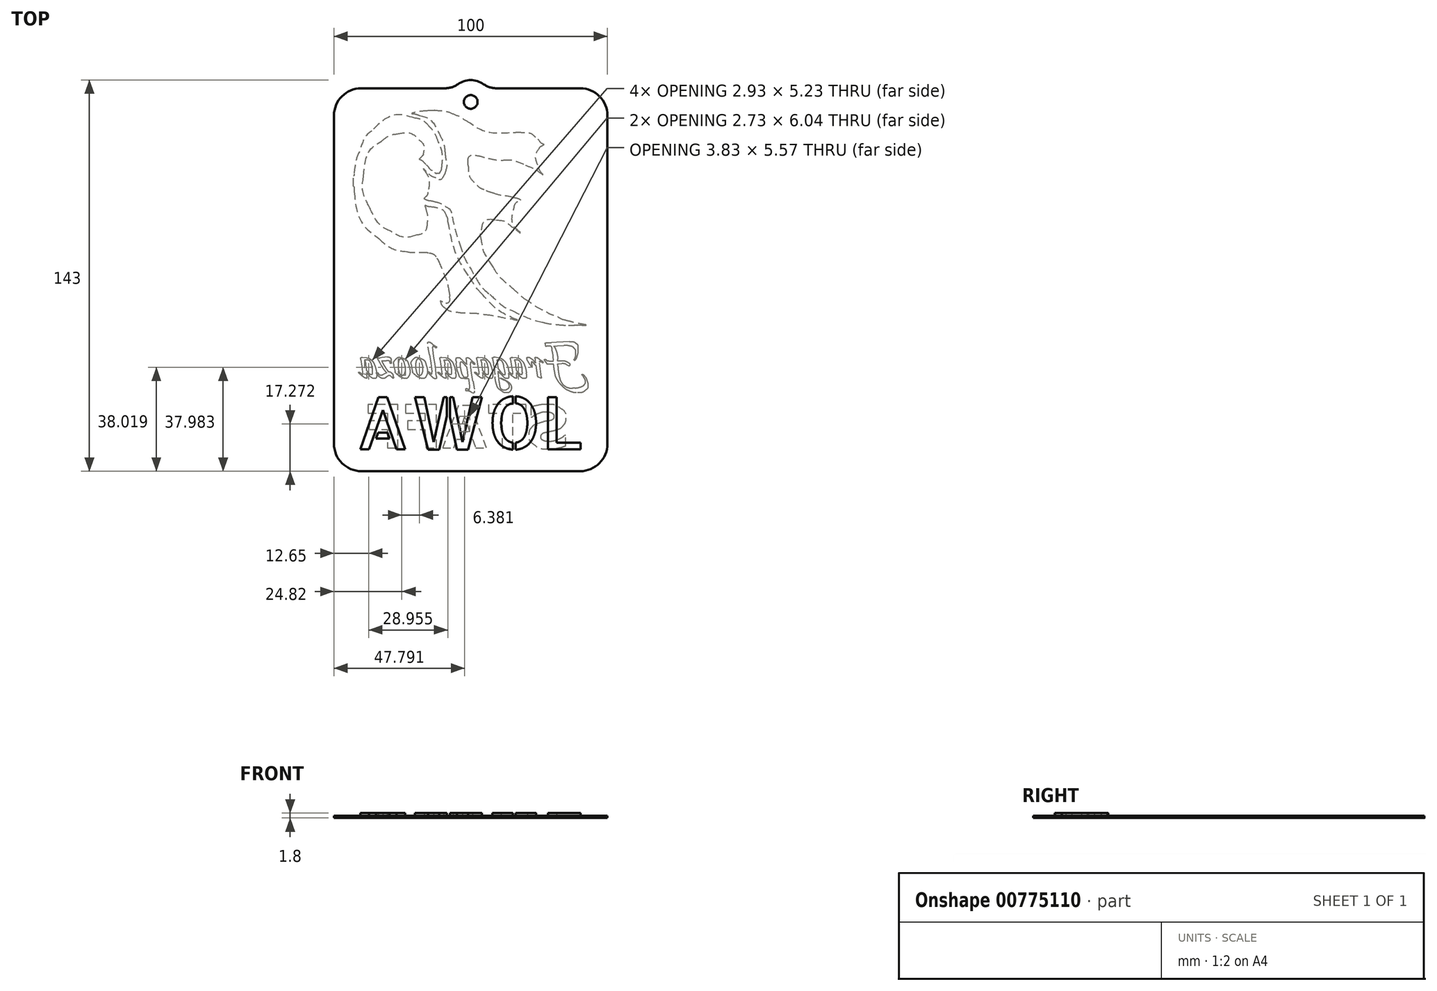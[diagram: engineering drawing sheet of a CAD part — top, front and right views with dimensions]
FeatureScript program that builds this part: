
annotation { "Feature Type Name" : "Feature", "Feature Type Description" : "" }
export const myFeature = defineFeature(function(context is Context, id is Id, definition is map)
    precondition{}
    {
        {
            var Q0;
            Q0=qCreatedBy(makeId("Top.planeOp"),FACE);
            var sketch = newSketch(context, id + "F0", { "sketchPlane" : qUnion([Q0])});
            skLineSegment(sketch, "E0.bottom", {"start": v(-40, 70) * mm, "end": v(-9.33, 70) * mm});
            skLineSegment(sketch, "E0.top", {"start": v(-40, -70) * mm, "end": v(40, -70) * mm});
            skLineSegment(sketch, "E0.left", {"start": v(-50, 60) * mm, "end": v(-50, -60) * mm});
            skLineSegment(sketch, "E0.right", {"start": v(50, 60) * mm, "end": v(50, -60) * mm});
            skPoint(sketch, "E0.middle", {"position": v(0, 0) * mm});
            skCircle(sketch, "E1", {"center": v(0, 65) * mm, "radius": 2.5 * mm});
            skPoint(sketch, "E2.visualSharp", {"position": v(-50, 70) * mm});
            skArc(sketch, "E2.filletArc", {"start": v(-40, 70) * mm, "mid": v(-47.07, 67.07) * mm, "end": v(-50, 60) * mm});
            skPoint(sketch, "E3.visualSharp", {"position": v(50, 70) * mm});
            skArc(sketch, "E3.filletArc", {"start": v(50, 60) * mm, "mid": v(47.07, 67.07) * mm, "end": v(40, 70) * mm});
            skPoint(sketch, "E4.visualSharp", {"position": v(50, -70) * mm});
            skArc(sketch, "E4.filletArc", {"start": v(40, -70) * mm, "mid": v(47.07, -67.07) * mm, "end": v(50, -60) * mm});
            skPoint(sketch, "E5.visualSharp", {"position": v(-50, -70) * mm});
            skArc(sketch, "E5.filletArc", {"start": v(-50, -60) * mm, "mid": v(-47.07, -67.07) * mm, "end": v(-40, -70) * mm});
            skArc(sketch, "E6", {"start": v(-4.66, 71.5) * mm, "mid": v(0, 73) * mm, "end": v(4.66, 71.5) * mm});
            skArc(sketch, "E7.filletArc", {"start": v(-9.33, 70) * mm, "mid": v(-6.88, 70.38) * mm, "end": v(-4.66, 71.5) * mm});
            skLineSegment(sketch, "E8", {"start": v(40, 70) * mm, "end": v(9.33, 70) * mm});
            skArc(sketch, "E9.filletArc", {"start": v(4.66, 71.5) * mm, "mid": v(6.88, 70.38) * mm, "end": v(9.33, 70) * mm});
            skSolve(sketch);
        }
        {
            var Q0;
            Q0=qCreatedBy(makeId("Top.planeOp"),FACE);
            var sketch = newSketch(context, id + "F1", { "sketchPlane" : qUnion([Q0])});
            skLineSegment(sketch, "E10", {"start": v(38.17, -16.7) * mm, "end": v(38.78, -16.7) * mm});
            skLineSegment(sketch, "E11", {"start": v(-13.07, 61.96) * mm, "end": v(-13.17, 61.96) * mm});
            skLineSegment(sketch, "E12", {"start": v(-14.17, 61.96) * mm, "end": v(-14.37, 61.96) * mm});
            skLineSegment(sketch, "E13", {"start": v(-42.85, 37.93) * mm, "end": v(-42.85, 36.81) * mm});
            skLineSegment(sketch, "E14", {"start": v(-42.85, 35.49) * mm, "end": v(-42.85, 34.98) * mm});
            skLineSegment(sketch, "E15", {"start": v(-42.85, 34.78) * mm, "end": v(-42.85, 34.16) * mm});
            skLineSegment(sketch, "E16", {"start": v(40.64, -16.7) * mm, "end": v(40.63, -16.62) * mm});
            skLineSegment(sketch, "E17", {"start": v(38.83, -16.7) * mm, "end": v(40.64, -16.7) * mm});
            skLineSegment(sketch, "E18", {"start": v(-42.85, 36.81) * mm, "end": v(-42.85, 35.49) * mm});
            skLineSegment(sketch, "E19", {"start": v(-13.21, 61.96) * mm, "end": v(-14.22, 61.96) * mm});
            skLineSegment(sketch, "E20", {"start": v(-42.85, 34.98) * mm, "end": v(-42.85, 34.77) * mm});
            skLineSegment(sketch, "E21", {"start": v(36.03, -31.52) * mm, "end": v(35.01, -30.98) * mm});
            skLineSegment(sketch, "E22", {"start": v(33.37, -30.7) * mm, "end": v(32.17, -30.75) * mm});
            skLineSegment(sketch, "E23", {"start": v(32.17, -30.75) * mm, "end": v(30.92, -30.82) * mm});
            skLineSegment(sketch, "E24", {"start": v(30.92, -30.82) * mm, "end": v(27.9, -30.82) * mm});
            skLineSegment(sketch, "E25", {"start": v(27.9, -30.82) * mm, "end": v(27.52, -30.26) * mm});
            skLineSegment(sketch, "E26", {"start": v(26.88, -29.35) * mm, "end": v(26.9, -29.28) * mm});
            skLineSegment(sketch, "E27", {"start": v(30.32, -29.76) * mm, "end": v(31.57, -29.76) * mm});
            skLineSegment(sketch, "E28", {"start": v(31.57, -29.76) * mm, "end": v(33.15, -29.76) * mm});
            skLineSegment(sketch, "E29", {"start": v(33.15, -29.76) * mm, "end": v(34.41, -29.76) * mm});
            skLineSegment(sketch, "E30", {"start": v(34.05, -24.06) * mm, "end": v(31.6, -24.16) * mm});
            skLineSegment(sketch, "E31", {"start": v(31.6, -24.16) * mm, "end": v(29.36, -24.3) * mm});
            skLineSegment(sketch, "E32", {"start": v(27.3, -24.39) * mm, "end": v(27.09, -23.13) * mm});
            skLineSegment(sketch, "E33", {"start": v(29.45, -22.97) * mm, "end": v(31.35, -22.93) * mm});
            skLineSegment(sketch, "E34", {"start": v(31.35, -22.93) * mm, "end": v(33.78, -22.78) * mm});
            skLineSegment(sketch, "E35", {"start": v(33.78, -22.78) * mm, "end": v(36.14, -22.66) * mm});
            skLineSegment(sketch, "E36", {"start": v(38.04, -29.5) * mm, "end": v(37.7, -29.32) * mm});
            skLineSegment(sketch, "E37", {"start": v(30.25, -30.2) * mm, "end": v(29.88, -26.54) * mm});
            skLineSegment(sketch, "E38", {"start": v(29.55, -24.56) * mm, "end": v(29.3, -24.3) * mm});
            skLineSegment(sketch, "E39", {"start": v(29.18, -23.96) * mm, "end": v(29.55, -24.04) * mm});
            skLineSegment(sketch, "E40", {"start": v(31.76, -29.06) * mm, "end": v(31.88, -31.82) * mm});
            skLineSegment(sketch, "E41", {"start": v(37.27, -39.71) * mm, "end": v(38.3, -39.63) * mm});
            skLineSegment(sketch, "E42", {"start": v(41.15, -35.4) * mm, "end": v(40.78, -34.92) * mm});
            skLineSegment(sketch, "E43", {"start": v(40.78, -34.92) * mm, "end": v(40.72, -34.76) * mm});
            skLineSegment(sketch, "E44", {"start": v(23.56, -29.53) * mm, "end": v(23.5, -28.89) * mm});
            skLineSegment(sketch, "E45", {"start": v(24.23, -28.54) * mm, "end": v(25.22, -29.23) * mm});
            skLineSegment(sketch, "E46", {"start": v(25.22, -29.23) * mm, "end": v(26.33, -30.01) * mm});
            skLineSegment(sketch, "E47", {"start": v(26.48, -30.3) * mm, "end": v(26.4, -30.34) * mm});
            skLineSegment(sketch, "E48", {"start": v(26.4, -30.34) * mm, "end": v(26.3, -30.32) * mm});
            skLineSegment(sketch, "E49", {"start": v(26.3, -30.32) * mm, "end": v(26.17, -30.3) * mm});
            skLineSegment(sketch, "E50", {"start": v(25.15, -30.3) * mm, "end": v(25.53, -33.54) * mm});
            skLineSegment(sketch, "E51", {"start": v(25.53, -33.54) * mm, "end": v(25.79, -35.64) * mm});
            skLineSegment(sketch, "E52", {"start": v(25.88, -36) * mm, "end": v(24.4, -35.44) * mm});
            skLineSegment(sketch, "E53", {"start": v(23.19, -29.85) * mm, "end": v(23.89, -30.75) * mm});
            skLineSegment(sketch, "E54", {"start": v(23.65, -31.18) * mm, "end": v(23.19, -30.77) * mm});
            skLineSegment(sketch, "E55", {"start": v(15.9, -29.4) * mm, "end": v(15.4, -29.4) * mm});
            skLineSegment(sketch, "E56", {"start": v(15.4, -29.4) * mm, "end": v(15.02, -29.33) * mm});
            skLineSegment(sketch, "E57", {"start": v(15.24, -28.42) * mm, "end": v(16.71, -28.55) * mm});
            skLineSegment(sketch, "E58", {"start": v(17.3, -34.56) * mm, "end": v(16.63, -33.84) * mm});
            skLineSegment(sketch, "E59", {"start": v(16.01, -32.3) * mm, "end": v(16.46, -32.84) * mm});
            skLineSegment(sketch, "E60", {"start": v(16.96, -29.4) * mm, "end": v(16.5, -29.4) * mm});
            skLineSegment(sketch, "E61", {"start": v(16.5, -29.4) * mm, "end": v(15.9, -29.4) * mm});
            skLineSegment(sketch, "E62", {"start": v(16.38, -31.1) * mm, "end": v(16.6, -32.79) * mm});
            skLineSegment(sketch, "E63", {"start": v(16.6, -32.79) * mm, "end": v(16.8, -34.4) * mm});
            skLineSegment(sketch, "E64", {"start": v(16.8, -34.4) * mm, "end": v(16.85, -35.3) * mm});
            skLineSegment(sketch, "E65", {"start": v(14.85, -34.45) * mm, "end": v(15.26, -34.75) * mm});
            skLineSegment(sketch, "E66", {"start": v(15.33, -34.51) * mm, "end": v(15.26, -33.72) * mm});
            skLineSegment(sketch, "E67", {"start": v(15.26, -33.72) * mm, "end": v(14.93, -31.64) * mm});
            skLineSegment(sketch, "E68", {"start": v(14.93, -31.64) * mm, "end": v(14.54, -29.14) * mm});
            skLineSegment(sketch, "E69", {"start": v(9.13, -29.4) * mm, "end": v(8.63, -29.4) * mm});
            skLineSegment(sketch, "E70", {"start": v(8.63, -29.4) * mm, "end": v(8.27, -29.31) * mm});
            skLineSegment(sketch, "E71", {"start": v(8.04, -29.08) * mm, "end": v(7.89, -28.74) * mm});
            skLineSegment(sketch, "E72", {"start": v(8.47, -28.35) * mm, "end": v(8.95, -28.35) * mm});
            skLineSegment(sketch, "E73", {"start": v(8.95, -28.35) * mm, "end": v(9.46, -28.52) * mm});
            skLineSegment(sketch, "E74", {"start": v(9.46, -28.52) * mm, "end": v(10.14, -28.6) * mm});
            skLineSegment(sketch, "E75", {"start": v(11.28, -34.74) * mm, "end": v(10.47, -33.88) * mm});
            skLineSegment(sketch, "E76", {"start": v(9.69, -32.05) * mm, "end": v(10.37, -32.95) * mm});
            skLineSegment(sketch, "E77", {"start": v(10.37, -32.95) * mm, "end": v(11.14, -33.94) * mm});
            skLineSegment(sketch, "E78", {"start": v(12.6, -34.13) * mm, "end": v(12.52, -33.32) * mm});
            skLineSegment(sketch, "E79", {"start": v(12.52, -33.32) * mm, "end": v(12.29, -32.26) * mm});
            skLineSegment(sketch, "E80", {"start": v(12.29, -32.26) * mm, "end": v(12.13, -31.6) * mm});
            skLineSegment(sketch, "E81", {"start": v(10.33, -29.4) * mm, "end": v(9.77, -29.4) * mm});
            skLineSegment(sketch, "E82", {"start": v(9.77, -29.4) * mm, "end": v(9.13, -29.4) * mm});
            skLineSegment(sketch, "E83", {"start": v(9.46, -28.84) * mm, "end": v(9.77, -30.97) * mm});
            skLineSegment(sketch, "E84", {"start": v(9.77, -30.97) * mm, "end": v(10.1, -34.04) * mm});
            skLineSegment(sketch, "E85", {"start": v(10.1, -34.04) * mm, "end": v(10.34, -36.29) * mm});
            skLineSegment(sketch, "E86", {"start": v(10.34, -36.29) * mm, "end": v(10.47, -37.68) * mm});
            skLineSegment(sketch, "E87", {"start": v(12.25, -36.7) * mm, "end": v(11.22, -36.28) * mm});
            skLineSegment(sketch, "E88", {"start": v(10.66, -36) * mm, "end": v(10.7, -35.94) * mm});
            skLineSegment(sketch, "E89", {"start": v(8.88, -35.3) * mm, "end": v(8.5, -31.75) * mm});
            skLineSegment(sketch, "E90", {"start": v(3.54, -29.4) * mm, "end": v(3.04, -29.4) * mm});
            skLineSegment(sketch, "E91", {"start": v(3.04, -29.4) * mm, "end": v(2.67, -29.33) * mm});
            skLineSegment(sketch, "E92", {"start": v(2.88, -28.42) * mm, "end": v(4.36, -28.55) * mm});
            skLineSegment(sketch, "E93", {"start": v(4.94, -34.56) * mm, "end": v(4.28, -33.84) * mm});
            skLineSegment(sketch, "E94", {"start": v(3.66, -32.3) * mm, "end": v(4.1, -32.84) * mm});
            skLineSegment(sketch, "E95", {"start": v(4.6, -29.4) * mm, "end": v(4.14, -29.4) * mm});
            skLineSegment(sketch, "E96", {"start": v(4.14, -29.4) * mm, "end": v(3.54, -29.4) * mm});
            skLineSegment(sketch, "E97", {"start": v(4.02, -31.1) * mm, "end": v(4.25, -32.79) * mm});
            skLineSegment(sketch, "E98", {"start": v(4.25, -32.79) * mm, "end": v(4.44, -34.4) * mm});
            skLineSegment(sketch, "E99", {"start": v(4.44, -34.4) * mm, "end": v(4.5, -35.3) * mm});
            skLineSegment(sketch, "E100", {"start": v(2.5, -34.45) * mm, "end": v(2.9, -34.75) * mm});
            skLineSegment(sketch, "E101", {"start": v(2.98, -34.51) * mm, "end": v(2.9, -33.72) * mm});
            skLineSegment(sketch, "E102", {"start": v(2.9, -33.72) * mm, "end": v(2.58, -31.64) * mm});
            skLineSegment(sketch, "E103", {"start": v(2.58, -31.64) * mm, "end": v(2.19, -29.14) * mm});
            skLineSegment(sketch, "E104", {"start": v(-0.07, -30.77) * mm, "end": v(0.03, -32.01) * mm});
            skLineSegment(sketch, "E105", {"start": v(0.03, -32.01) * mm, "end": v(0.35, -34.14) * mm});
            skLineSegment(sketch, "E106", {"start": v(0.35, -34.14) * mm, "end": v(0.85, -37.11) * mm});
            skLineSegment(sketch, "E107", {"start": v(0.96, -41.4) * mm, "end": v(0.32, -41.16) * mm});
            skLineSegment(sketch, "E108", {"start": v(-0.43, -39.67) * mm, "end": v(-0.47, -38.83) * mm});
            skLineSegment(sketch, "E109", {"start": v(-0.47, -38.83) * mm, "end": v(-0.77, -36.7) * mm});
            skLineSegment(sketch, "E110", {"start": v(-0.77, -36.7) * mm, "end": v(-1.14, -33.74) * mm});
            skLineSegment(sketch, "E111", {"start": v(-1.14, -33.74) * mm, "end": v(-1.34, -32.16) * mm});
            skLineSegment(sketch, "E112", {"start": v(-1.34, -32.16) * mm, "end": v(-1.56, -30.34) * mm});
            skLineSegment(sketch, "E113", {"start": v(-1.56, -30.34) * mm, "end": v(-1.62, -29.37) * mm});
            skLineSegment(sketch, "E114", {"start": v(-0.41, -35.45) * mm, "end": v(-0.36, -35.65) * mm});
            skLineSegment(sketch, "E115", {"start": v(-0.18, -36.1) * mm, "end": v(-0.24, -36.16) * mm});
            skLineSegment(sketch, "E116", {"start": v(-0.24, -36.16) * mm, "end": v(-0.31, -36.19) * mm});
            skLineSegment(sketch, "E117", {"start": v(-0.31, -36.19) * mm, "end": v(-0.7, -36.11) * mm});
            skLineSegment(sketch, "E118", {"start": v(-0.7, -36.11) * mm, "end": v(-1.4, -36.11) * mm});
            skLineSegment(sketch, "E119", {"start": v(-1.4, -36.11) * mm, "end": v(-2.27, -36.11) * mm});
            skLineSegment(sketch, "E120", {"start": v(-2.53, -30.03) * mm, "end": v(-1.85, -30.67) * mm});
            skLineSegment(sketch, "E121", {"start": v(-9.94, -29.4) * mm, "end": v(-10.44, -29.4) * mm});
            skLineSegment(sketch, "E122", {"start": v(-10.44, -29.4) * mm, "end": v(-10.8, -29.33) * mm});
            skLineSegment(sketch, "E123", {"start": v(-10.6, -28.42) * mm, "end": v(-9.12, -28.55) * mm});
            skLineSegment(sketch, "E124", {"start": v(-8.54, -34.56) * mm, "end": v(-9.2, -33.84) * mm});
            skLineSegment(sketch, "E125", {"start": v(-9.82, -32.3) * mm, "end": v(-9.37, -32.84) * mm});
            skLineSegment(sketch, "E126", {"start": v(-8.87, -29.4) * mm, "end": v(-9.34, -29.4) * mm});
            skLineSegment(sketch, "E127", {"start": v(-9.34, -29.4) * mm, "end": v(-9.94, -29.4) * mm});
            skLineSegment(sketch, "E128", {"start": v(-9.46, -31.1) * mm, "end": v(-9.23, -32.79) * mm});
            skLineSegment(sketch, "E129", {"start": v(-9.23, -32.79) * mm, "end": v(-9.04, -34.4) * mm});
            skLineSegment(sketch, "E130", {"start": v(-9.04, -34.4) * mm, "end": v(-8.99, -35.3) * mm});
            skLineSegment(sketch, "E131", {"start": v(-10.98, -34.45) * mm, "end": v(-10.58, -34.75) * mm});
            skLineSegment(sketch, "E132", {"start": v(-10.5, -34.51) * mm, "end": v(-10.58, -33.72) * mm});
            skLineSegment(sketch, "E133", {"start": v(-10.58, -33.72) * mm, "end": v(-10.9, -31.64) * mm});
            skLineSegment(sketch, "E134", {"start": v(-10.9, -31.64) * mm, "end": v(-11.29, -29.14) * mm});
            skLineSegment(sketch, "E135", {"start": v(-14.16, -33.74) * mm, "end": v(-14.26, -32.52) * mm});
            skLineSegment(sketch, "E136", {"start": v(-14.26, -32.52) * mm, "end": v(-14.56, -30.46) * mm});
            skLineSegment(sketch, "E137", {"start": v(-14.56, -30.46) * mm, "end": v(-15.08, -27.43) * mm});
            skLineSegment(sketch, "E138", {"start": v(-15, -22.92) * mm, "end": v(-14.03, -23.56) * mm});
            skLineSegment(sketch, "E139", {"start": v(-12.63, -24.87) * mm, "end": v(-12.86, -24.8) * mm});
            skLineSegment(sketch, "E140", {"start": v(-13.91, -24.76) * mm, "end": v(-13.85, -25.5) * mm});
            skLineSegment(sketch, "E141", {"start": v(-13.85, -25.5) * mm, "end": v(-13.65, -26.9) * mm});
            skLineSegment(sketch, "E142", {"start": v(-13.65, -26.9) * mm, "end": v(-13.36, -28.73) * mm});
            skLineSegment(sketch, "E143", {"start": v(-13.36, -28.73) * mm, "end": v(-13.08, -30.79) * mm});
            skLineSegment(sketch, "E144", {"start": v(-13.08, -30.79) * mm, "end": v(-12.8, -32.84) * mm});
            skLineSegment(sketch, "E145", {"start": v(-12.8, -32.84) * mm, "end": v(-12.61, -34.45) * mm});
            skLineSegment(sketch, "E146", {"start": v(-12.61, -34.45) * mm, "end": v(-12.55, -35.39) * mm});
            skLineSegment(sketch, "E147", {"start": v(-19.13, -35.54) * mm, "end": v(-20.12, -34.9) * mm});
            skLineSegment(sketch, "E148", {"start": v(-21.26, -33.55) * mm, "end": v(-21.5, -32.5) * mm});
            skLineSegment(sketch, "E149", {"start": v(-21.5, -32.5) * mm, "end": v(-21.73, -31.52) * mm});
            skLineSegment(sketch, "E150", {"start": v(-21.73, -31.52) * mm, "end": v(-21.79, -30.84) * mm});
            skLineSegment(sketch, "E151", {"start": v(-19.8, -28.37) * mm, "end": v(-19.36, -28.42) * mm});
            skLineSegment(sketch, "E152", {"start": v(-19.36, -28.42) * mm, "end": v(-18.37, -28.75) * mm});
            skLineSegment(sketch, "E153", {"start": v(-17.54, -31.66) * mm, "end": v(-18, -30.05) * mm});
            skLineSegment(sketch, "E154", {"start": v(-25.5, -35.54) * mm, "end": v(-26.5, -34.9) * mm});
            skLineSegment(sketch, "E155", {"start": v(-27.64, -33.55) * mm, "end": v(-27.88, -32.5) * mm});
            skLineSegment(sketch, "E156", {"start": v(-27.88, -32.5) * mm, "end": v(-28.1, -31.52) * mm});
            skLineSegment(sketch, "E157", {"start": v(-28.1, -31.52) * mm, "end": v(-28.17, -30.84) * mm});
            skLineSegment(sketch, "E158", {"start": v(-26.19, -28.37) * mm, "end": v(-25.74, -28.42) * mm});
            skLineSegment(sketch, "E159", {"start": v(-25.74, -28.42) * mm, "end": v(-24.75, -28.75) * mm});
            skLineSegment(sketch, "E160", {"start": v(-23.92, -31.66) * mm, "end": v(-24.38, -30.05) * mm});
            skLineSegment(sketch, "E161", {"start": v(-30.82, -29.63) * mm, "end": v(-31.6, -29.66) * mm});
            skLineSegment(sketch, "E162", {"start": v(-31.6, -29.66) * mm, "end": v(-32.28, -29.63) * mm});
            skLineSegment(sketch, "E163", {"start": v(-32.28, -29.63) * mm, "end": v(-32.6, -29.59) * mm});
            skLineSegment(sketch, "E164", {"start": v(-28.05, -35.7) * mm, "end": v(-28.34, -36) * mm});
            skLineSegment(sketch, "E165", {"start": v(-32.16, -32.19) * mm, "end": v(-32.67, -31.4) * mm});
            skLineSegment(sketch, "E166", {"start": v(-32.67, -31.4) * mm, "end": v(-33.23, -30.44) * mm});
            skLineSegment(sketch, "E167", {"start": v(-33.23, -30.44) * mm, "end": v(-33.8, -29.45) * mm});
            skLineSegment(sketch, "E168", {"start": v(-33.8, -29.45) * mm, "end": v(-34.28, -28.64) * mm});
            skLineSegment(sketch, "E169", {"start": v(-34.18, -28.33) * mm, "end": v(-34.02, -28.38) * mm});
            skLineSegment(sketch, "E170", {"start": v(-33.17, -28.56) * mm, "end": v(-32.43, -28.52) * mm});
            skLineSegment(sketch, "E171", {"start": v(-32.43, -28.52) * mm, "end": v(-31.52, -28.4) * mm});
            skLineSegment(sketch, "E172", {"start": v(-31.52, -28.4) * mm, "end": v(-30.4, -28.23) * mm});
            skLineSegment(sketch, "E173", {"start": v(-29.1, -29.33) * mm, "end": v(-29.02, -30) * mm});
            skLineSegment(sketch, "E174", {"start": v(-28.09, -35.68) * mm, "end": v(-28.22, -35.85) * mm});
            skLineSegment(sketch, "E175", {"start": v(-28.4, -35.95) * mm, "end": v(-29.27, -35.27) * mm});
            skLineSegment(sketch, "E176", {"start": v(-32.12, -34.67) * mm, "end": v(-31.13, -34.22) * mm});
            skLineSegment(sketch, "E177", {"start": v(-31.13, -34.22) * mm, "end": v(-30.22, -33.8) * mm});
            skLineSegment(sketch, "E178", {"start": v(-28.36, -35.08) * mm, "end": v(-28.32, -35.29) * mm});
            skLineSegment(sketch, "E179", {"start": v(-28.32, -35.29) * mm, "end": v(-28.26, -35.48) * mm});
            skLineSegment(sketch, "E180", {"start": v(-28.26, -35.48) * mm, "end": v(-28.09, -35.68) * mm});
            skLineSegment(sketch, "E181", {"start": v(-38.9, -29.4) * mm, "end": v(-39.4, -29.4) * mm});
            skLineSegment(sketch, "E182", {"start": v(-39.4, -29.4) * mm, "end": v(-39.76, -29.33) * mm});
            skLineSegment(sketch, "E183", {"start": v(-39.55, -28.42) * mm, "end": v(-38.08, -28.55) * mm});
            skLineSegment(sketch, "E184", {"start": v(-37.5, -34.56) * mm, "end": v(-38.15, -33.84) * mm});
            skLineSegment(sketch, "E185", {"start": v(-38.77, -32.3) * mm, "end": v(-38.33, -32.84) * mm});
            skLineSegment(sketch, "E186", {"start": v(-37.82, -29.4) * mm, "end": v(-38.3, -29.4) * mm});
            skLineSegment(sketch, "E187", {"start": v(-38.3, -29.4) * mm, "end": v(-38.9, -29.4) * mm});
            skLineSegment(sketch, "E188", {"start": v(-38.41, -31.1) * mm, "end": v(-38.19, -32.79) * mm});
            skLineSegment(sketch, "E189", {"start": v(-38.19, -32.79) * mm, "end": v(-38, -34.4) * mm});
            skLineSegment(sketch, "E190", {"start": v(-38, -34.4) * mm, "end": v(-37.94, -35.3) * mm});
            skLineSegment(sketch, "E191", {"start": v(-39.94, -34.45) * mm, "end": v(-39.53, -34.75) * mm});
            skLineSegment(sketch, "E192", {"start": v(-39.45, -34.51) * mm, "end": v(-39.53, -33.72) * mm});
            skLineSegment(sketch, "E193", {"start": v(-39.53, -33.72) * mm, "end": v(-39.86, -31.64) * mm});
            skLineSegment(sketch, "E194", {"start": v(-39.86, -31.64) * mm, "end": v(-40.24, -29.14) * mm});
            skLineSegment(sketch, "E195", {"start": v(22.49, -50.22) * mm, "end": v(22.06, -50.22) * mm});
            skLineSegment(sketch, "E196", {"start": v(22.06, -50.22) * mm, "end": v(22.06, -46.56) * mm});
            skLineSegment(sketch, "E197", {"start": v(34.32, -56.92) * mm, "end": v(34.76, -56.92) * mm});
            skLineSegment(sketch, "E198", {"start": v(34.76, -56.92) * mm, "end": v(34.76, -60.73) * mm});
            skLineSegment(sketch, "E199", {"start": v(6.54, -45.64) * mm, "end": v(20.3, -45.64) * mm});
            skLineSegment(sketch, "E200", {"start": v(20.3, -45.64) * mm, "end": v(20.3, -48.81) * mm});
            skLineSegment(sketch, "E201", {"start": v(20.3, -48.81) * mm, "end": v(15.36, -48.81) * mm});
            skLineSegment(sketch, "E202", {"start": v(15.36, -48.81) * mm, "end": v(15.36, -61.51) * mm});
            skLineSegment(sketch, "E203", {"start": v(15.36, -61.51) * mm, "end": v(11.47, -61.51) * mm});
            skLineSegment(sketch, "E204", {"start": v(11.47, -61.51) * mm, "end": v(11.47, -48.81) * mm});
            skLineSegment(sketch, "E205", {"start": v(11.47, -48.81) * mm, "end": v(6.54, -48.81) * mm});
            skLineSegment(sketch, "E206", {"start": v(6.54, -48.81) * mm, "end": v(6.54, -45.64) * mm});
            skLineSegment(sketch, "E207", {"start": v(-4.56, -45.99) * mm, "end": v(0.04, -45.99) * mm});
            skLineSegment(sketch, "E208", {"start": v(0.04, -45.99) * mm, "end": v(5.78, -61.51) * mm});
            skLineSegment(sketch, "E209", {"start": v(5.78, -61.51) * mm, "end": v(1.8, -61.51) * mm});
            skLineSegment(sketch, "E210", {"start": v(1.8, -61.51) * mm, "end": v(0.7, -58.34) * mm});
            skLineSegment(sketch, "E211", {"start": v(0.7, -58.34) * mm, "end": v(-5.12, -58.34) * mm});
            skLineSegment(sketch, "E212", {"start": v(-5.12, -58.34) * mm, "end": v(-6.2, -61.51) * mm});
            skLineSegment(sketch, "E213", {"start": v(-6.2, -61.51) * mm, "end": v(-10.3, -61.51) * mm});
            skLineSegment(sketch, "E214", {"start": v(-10.3, -61.51) * mm, "end": v(-4.56, -45.99) * mm});
            skLineSegment(sketch, "E215", {"start": v(-0.3, -55.51) * mm, "end": v(-2.2, -49.94) * mm});
            skLineSegment(sketch, "E216", {"start": v(-2.2, -49.94) * mm, "end": v(-4.12, -55.51) * mm});
            skLineSegment(sketch, "E217", {"start": v(-4.12, -55.51) * mm, "end": v(-0.3, -55.51) * mm});
            skLineSegment(sketch, "E218", {"start": v(-23.8, -45.64) * mm, "end": v(-12.51, -45.64) * mm});
            skLineSegment(sketch, "E219", {"start": v(-12.51, -45.64) * mm, "end": v(-12.51, -61.51) * mm});
            skLineSegment(sketch, "E220", {"start": v(-12.51, -61.51) * mm, "end": v(-16.4, -61.51) * mm});
            skLineSegment(sketch, "E221", {"start": v(-16.4, -61.51) * mm, "end": v(-16.75, -54.8) * mm});
            skLineSegment(sketch, "E222", {"start": v(-16.75, -54.8) * mm, "end": v(-23.1, -54.8) * mm});
            skLineSegment(sketch, "E223", {"start": v(-23.1, -54.8) * mm, "end": v(-23.1, -51.63) * mm});
            skLineSegment(sketch, "E224", {"start": v(-23.1, -51.63) * mm, "end": v(-16.75, -51.63) * mm});
            skLineSegment(sketch, "E225", {"start": v(-16.75, -51.63) * mm, "end": v(-16.75, -48.81) * mm});
            skLineSegment(sketch, "E226", {"start": v(-16.75, -48.81) * mm, "end": v(-23.8, -48.81) * mm});
            skLineSegment(sketch, "E227", {"start": v(-23.8, -48.81) * mm, "end": v(-23.8, -45.64) * mm});
            skLineSegment(sketch, "E228", {"start": v(-37.56, -45.64) * mm, "end": v(-26.63, -45.64) * mm});
            skLineSegment(sketch, "E229", {"start": v(-26.63, -45.64) * mm, "end": v(-26.63, -61.51) * mm});
            skLineSegment(sketch, "E230", {"start": v(-26.63, -61.51) * mm, "end": v(-30.5, -61.51) * mm});
            skLineSegment(sketch, "E231", {"start": v(-30.5, -61.51) * mm, "end": v(-30.5, -54.8) * mm});
            skLineSegment(sketch, "E232", {"start": v(-30.5, -54.8) * mm, "end": v(-37.2, -54.8) * mm});
            skLineSegment(sketch, "E233", {"start": v(-37.2, -54.8) * mm, "end": v(-37.2, -51.63) * mm});
            skLineSegment(sketch, "E234", {"start": v(-37.2, -51.63) * mm, "end": v(-30.5, -51.63) * mm});
            skLineSegment(sketch, "E235", {"start": v(-30.5, -51.63) * mm, "end": v(-30.5, -48.81) * mm});
            skLineSegment(sketch, "E236", {"start": v(-30.5, -48.81) * mm, "end": v(-37.56, -48.81) * mm});
            skLineSegment(sketch, "E237", {"start": v(-37.56, -48.81) * mm, "end": v(-37.56, -45.64) * mm});
            skFitSpline(sketch, "E238", {"points": [v(-14.37, 61.96) * mm, v(-14.8, 61.78) * mm, v(-15.26, 61.8) * mm, v(-15.71, 61.76) * mm]});
            skFitSpline(sketch, "E239", {"points": [v(-15.71, 61.76) * mm, v(-17.53, 61.62) * mm, v(-19.32, 61.38) * mm, v(-21.1, 60.93) * mm]});
            skFitSpline(sketch, "E240", {"points": [v(-21.1, 60.93) * mm, v(-21.24, 60.9) * mm, v(-21.43, 60.9) * mm, v(-21.54, 60.66) * mm]});
            skFitSpline(sketch, "E241", {"points": [v(-21.54, 60.66) * mm, v(-20.54, 60.63) * mm, v(-19.62, 60.35) * mm, v(-18.7, 60.03) * mm]});
            skFitSpline(sketch, "E242", {"points": [v(-18.7, 60.03) * mm, v(-15.38, 58.87) * mm, v(-13.15, 56.52) * mm, v(-11.58, 53.44) * mm]});
            skFitSpline(sketch, "E243", {"points": [v(-11.58, 53.44) * mm, v(-10.47, 51.29) * mm, v(-9.71, 49) * mm, v(-9.41, 46.6) * mm]});
            skFitSpline(sketch, "E244", {"points": [v(-9.41, 46.6) * mm, v(-9.11, 44.15) * mm, v(-8.77, 41.68) * mm, v(-9.35, 39.2) * mm]});
            skFitSpline(sketch, "E245", {"points": [v(-9.35, 39.2) * mm, v(-9.4, 38.94) * mm, v(-9.5, 38.7) * mm, v(-9.63, 38.47) * mm]});
            skFitSpline(sketch, "E246", {"points": [v(-9.63, 38.47) * mm, v(-10.22, 37.39) * mm, v(-11.1, 36.57) * mm, v(-12.72, 37.2) * mm]});
            skFitSpline(sketch, "E247", {"points": [v(-12.72, 37.2) * mm, v(-14.12, 37.75) * mm, v(-15.28, 38.64) * mm, v(-16.36, 39.65) * mm]});
            skFitSpline(sketch, "E248", {"points": [v(-16.36, 39.65) * mm, v(-16.66, 39.92) * mm, v(-16.91, 40.23) * mm, v(-17.25, 40.59) * mm]});
            skFitSpline(sketch, "E249", {"points": [v(-17.25, 40.59) * mm, v(-17.26, 40.3) * mm, v(-17.11, 40.19) * mm, v(-17.03, 40.05) * mm]});
            skFitSpline(sketch, "E250", {"points": [v(-17.03, 40.05) * mm, v(-15.47, 37.53) * mm, v(-15.17, 34.78) * mm, v(-15.68, 31.91) * mm]});
            skFitSpline(sketch, "E251", {"points": [v(-15.68, 31.91) * mm, v(-15.8, 31.24) * mm, v(-16.1, 30.64) * mm, v(-16.6, 30.16) * mm]});
            skFitSpline(sketch, "E252", {"points": [v(-16.6, 30.16) * mm, v(-17.12, 29.67) * mm, v(-17.1, 29.65) * mm, v(-16.44, 29.37) * mm]});
            skFitSpline(sketch, "E253", {"points": [v(-16.44, 29.37) * mm, v(-15.51, 28.97) * mm, v(-14.51, 28.87) * mm, v(-13.54, 28.62) * mm]});
            skFitSpline(sketch, "E254", {"points": [v(-13.54, 28.62) * mm, v(-11.87, 28.2) * mm, v(-10.3, 27.56) * mm, v(-8.86, 26.56) * mm]});
            skFitSpline(sketch, "E255", {"points": [v(-8.86, 26.56) * mm, v(-7.66, 25.72) * mm, v(-7.05, 24.5) * mm, v(-6.77, 23.12) * mm]});
            skFitSpline(sketch, "E256", {"points": [v(-6.77, 23.12) * mm, v(-6.07, 19.68) * mm, v(-5.15, 16.3) * mm, v(-4.03, 13) * mm]});
            skFitSpline(sketch, "E257", {"points": [v(-4.03, 13) * mm, v(-3.06, 10.12) * mm, v(-1.94, 7.3) * mm, v(-0.43, 4.69) * mm]});
            skFitSpline(sketch, "E258", {"points": [v(-0.43, 4.69) * mm, v(1.68, 1.04) * mm, v(3.89, -2.54) * mm, v(7.02, -5.42) * mm]});
            skFitSpline(sketch, "E259", {"points": [v(7.02, -5.42) * mm, v(9.48, -7.68) * mm, v(12.02, -9.8) * mm, v(15.04, -11.25) * mm]});
            skFitSpline(sketch, "E260", {"points": [v(15.04, -11.25) * mm, v(18.76, -13.03) * mm, v(22.58, -14.59) * mm, v(26.59, -15.61) * mm]});
            skFitSpline(sketch, "E261", {"points": [v(26.59, -15.61) * mm, v(28.25, -16.04) * mm, v(29.96, -16.23) * mm, v(31.67, -16.4) * mm]});
            skFitSpline(sketch, "E262", {"points": [v(31.67, -16.4) * mm, v(33.03, -16.54) * mm, v(34.4, -16.62) * mm, v(35.77, -16.62) * mm]});
            skFitSpline(sketch, "E263", {"points": [v(35.77, -16.62) * mm, v(36.22, -16.7) * mm, v(36.67, -16.64) * mm, v(37.13, -16.66) * mm]});
            skFitSpline(sketch, "E264", {"points": [v(37.13, -16.66) * mm, v(37.48, -16.68) * mm, v(37.83, -16.6) * mm, v(38.17, -16.7) * mm]});
            skFitSpline(sketch, "E265", {"points": [v(38.78, -16.7) * mm, v(39.38, -16.6) * mm, v(39.99, -16.69) * mm, v(40.59, -16.66) * mm]});
            skFitSpline(sketch, "E266", {"points": [v(40.59, -16.66) * mm, v(41.03, -16.65) * mm, v(41.48, -16.66) * mm, v(41.92, -16.65) * mm]});
            skFitSpline(sketch, "E267", {"points": [v(41.92, -16.65) * mm, v(42.02, -16.65) * mm, v(42.17, -16.71) * mm, v(42.18, -16.52) * mm]});
            skFitSpline(sketch, "E268", {"points": [v(42.18, -16.52) * mm, v(40.35, -16.18) * mm, v(38.52, -15.83) * mm, v(36.71, -15.35) * mm]});
            skFitSpline(sketch, "E269", {"points": [v(36.71, -15.35) * mm, v(36, -15.16) * mm, v(35.25, -15.03) * mm, v(34.53, -14.82) * mm]});
            skFitSpline(sketch, "E270", {"points": [v(34.53, -14.82) * mm, v(33.1, -14.38) * mm, v(31.81, -13.6) * mm, v(30.4, -13.1) * mm]});
            skFitSpline(sketch, "E271", {"points": [v(30.4, -13.1) * mm, v(28.9, -12.57) * mm, v(27.54, -11.75) * mm, v(26.13, -11.04) * mm]});
            skFitSpline(sketch, "E272", {"points": [v(26.13, -11.04) * mm, v(24.28, -10.1) * mm, v(22.61, -8.9) * mm, v(20.9, -7.78) * mm]});
            skFitSpline(sketch, "E273", {"points": [v(20.9, -7.78) * mm, v(19.32, -6.73) * mm, v(17.87, -5.46) * mm, v(16.43, -4.2) * mm]});
            skFitSpline(sketch, "E274", {"points": [v(16.43, -4.2) * mm, v(13.43, -1.57) * mm, v(10.5, 1.14) * mm, v(8.29, 4.51) * mm]});
            skFitSpline(sketch, "E275", {"points": [v(8.29, 4.51) * mm, v(6.39, 7.4) * mm, v(4.75, 10.42) * mm, v(4.04, 13.87) * mm]});
            skFitSpline(sketch, "E276", {"points": [v(4.04, 13.87) * mm, v(3.74, 15.29) * mm, v(3.6, 16.77) * mm, v(3.96, 18.15) * mm]});
            skFitSpline(sketch, "E277", {"points": [v(3.96, 18.15) * mm, v(4.68, 20.94) * mm, v(6.59, 22.1) * mm, v(9.37, 21.76) * mm]});
            skFitSpline(sketch, "E278", {"points": [v(9.37, 21.76) * mm, v(12.14, 21.42) * mm, v(14.36, 19.9) * mm, v(16.53, 18.28) * mm]});
            skFitSpline(sketch, "E279", {"points": [v(16.53, 18.28) * mm, v(17.05, 17.9) * mm, v(17.55, 17.5) * mm, v(18.06, 17.1) * mm]});
            skFitSpline(sketch, "E280", {"points": [v(18.06, 17.1) * mm, v(18.14, 17.24) * mm, v(18.06, 17.27) * mm, v(18.02, 17.3) * mm]});
            skFitSpline(sketch, "E281", {"points": [v(18.02, 17.3) * mm, v(15.67, 19.8) * mm, v(15.1, 22.76) * mm, v(15.81, 26.03) * mm]});
            skFitSpline(sketch, "E282", {"points": [v(15.81, 26.03) * mm, v(16.12, 27.45) * mm, v(16.96, 28.48) * mm, v(18.36, 29.08) * mm]});
            skFitSpline(sketch, "E283", {"points": [v(18.36, 29.08) * mm, v(17.45, 29.57) * mm, v(16.52, 29.83) * mm, v(15.58, 30.04) * mm]});
            skFitSpline(sketch, "E284", {"points": [v(15.58, 30.04) * mm, v(13.22, 30.57) * mm, v(10.83, 30.9) * mm, v(8.5, 31.57) * mm]});
            skFitSpline(sketch, "E285", {"points": [v(8.5, 31.57) * mm, v(7.27, 31.92) * mm, v(6.07, 32.36) * mm, v(4.9, 32.88) * mm]});
            skFitSpline(sketch, "E286", {"points": [v(4.9, 32.88) * mm, v(3.5, 33.5) * mm, v(2.36, 34.42) * mm, v(1.34, 35.53) * mm]});
            skFitSpline(sketch, "E287", {"points": [v(1.34, 35.53) * mm, v(0.04, 36.96) * mm, v(-0.59, 38.66) * mm, v(-0.74, 40.57) * mm]});
            skFitSpline(sketch, "E288", {"points": [v(-0.74, 40.57) * mm, v(-0.8, 41.38) * mm, v(-1, 42.17) * mm, v(-0.94, 43) * mm]});
            skFitSpline(sketch, "E289", {"points": [v(-0.94, 43) * mm, v(-0.85, 44.55) * mm, v(0.53, 45.67) * mm, v(2.04, 45.42) * mm]});
            skFitSpline(sketch, "E290", {"points": [v(2.04, 45.42) * mm, v(3.57, 45.16) * mm, v(5.04, 44.69) * mm, v(6.55, 44.35) * mm]});
            skFitSpline(sketch, "E291", {"points": [v(6.55, 44.35) * mm, v(8.37, 43.95) * mm, v(10.2, 43.7) * mm, v(12.06, 43.72) * mm]});
            skFitSpline(sketch, "E292", {"points": [v(12.06, 43.72) * mm, v(14.87, 43.77) * mm, v(17.47, 42.99) * mm, v(20.03, 41.9) * mm]});
            skFitSpline(sketch, "E293", {"points": [v(20.03, 41.9) * mm, v(22.15, 41) * mm, v(24.19, 39.94) * mm, v(26.08, 38.6) * mm]});
            skFitSpline(sketch, "E294", {"points": [v(26.08, 38.6) * mm, v(26.17, 38.53) * mm, v(26.25, 38.43) * mm, v(26.44, 38.49) * mm]});
            skFitSpline(sketch, "E295", {"points": [v(26.44, 38.49) * mm, v(25.56, 39.48) * mm, v(24.9, 40.61) * mm, v(24.5, 41.84) * mm]});
            skFitSpline(sketch, "E296", {"points": [v(24.5, 41.84) * mm, v(23.83, 43.93) * mm, v(23.78, 46.02) * mm, v(25.03, 47.97) * mm]});
            skFitSpline(sketch, "E297", {"points": [v(25.03, 47.97) * mm, v(25.46, 48.64) * mm, v(26.12, 49) * mm, v(26.82, 49.4) * mm]});
            skFitSpline(sketch, "E298", {"points": [v(26.82, 49.4) * mm, v(25.63, 50.1) * mm, v(24.78, 51.15) * mm, v(23.76, 52) * mm]});
            skFitSpline(sketch, "E299", {"points": [v(23.76, 52) * mm, v(22.25, 53.27) * mm, v(20.44, 53.7) * mm, v(18.55, 53.75) * mm]});
            skFitSpline(sketch, "E300", {"points": [v(18.55, 53.75) * mm, v(17.1, 53.78) * mm, v(15.64, 53.72) * mm, v(14.19, 53.67) * mm]});
            skFitSpline(sketch, "E301", {"points": [v(14.19, 53.67) * mm, v(9.06, 53.52) * mm, v(4.2, 54.58) * mm, v(-0.26, 57.24) * mm]});
            skFitSpline(sketch, "E302", {"points": [v(-0.26, 57.24) * mm, v(-2.15, 58.37) * mm, v(-4.03, 59.52) * mm, v(-6.07, 60.37) * mm]});
            skFitSpline(sketch, "E303", {"points": [v(-6.07, 60.37) * mm, v(-8.01, 61.18) * mm, v(-10.04, 61.62) * mm, v(-12.13, 61.77) * mm]});
            skFitSpline(sketch, "E304", {"points": [v(-12.13, 61.77) * mm, v(-12.45, 61.8) * mm, v(-12.78, 61.8) * mm, v(-13.07, 61.96) * mm]});
            skFitSpline(sketch, "E305", {"points": [v(-13.17, 61.96) * mm, v(-13.5, 61.88) * mm, v(-13.84, 61.88) * mm, v(-14.17, 61.96) * mm]});
            skFitSpline(sketch, "E306", {"points": [v(-42.85, 34.16) * mm, v(-42.6, 33.55) * mm, v(-42.66, 32.89) * mm, v(-42.57, 32.25) * mm]});
            skFitSpline(sketch, "E307", {"points": [v(-42.57, 32.25) * mm, v(-41.63, 25.4) * mm, v(-38.8, 19.57) * mm, v(-33.58, 15.04) * mm]});
            skFitSpline(sketch, "E308", {"points": [v(-33.58, 15.04) * mm, v(-30.64, 12.5) * mm, v(-27.24, 10.89) * mm, v(-23.4, 10.27) * mm]});
            skFitSpline(sketch, "E309", {"points": [v(-23.4, 10.27) * mm, v(-21.75, 10) * mm, v(-20.07, 10.08) * mm, v(-18.4, 10.01) * mm]});
            skFitSpline(sketch, "E310", {"points": [v(-18.4, 10.01) * mm, v(-17.32, 9.97) * mm, v(-16.24, 9.98) * mm, v(-15.16, 9.75) * mm]});
            skFitSpline(sketch, "E311", {"points": [v(-15.16, 9.75) * mm, v(-13.94, 9.5) * mm, v(-13.02, 8.84) * mm, v(-12.34, 7.82) * mm]});
            skFitSpline(sketch, "E312", {"points": [v(-12.34, 7.82) * mm, v(-12.12, 7.48) * mm, v(-11.9, 7.13) * mm, v(-11.74, 6.76) * mm]});
            skFitSpline(sketch, "E313", {"points": [v(-11.74, 6.76) * mm, v(-10.3, 3.3) * mm, v(-8.86, -0.17) * mm, v(-8.04, -3.86) * mm]});
            skFitSpline(sketch, "E314", {"points": [v(-8.04, -3.86) * mm, v(-7.85, -4.74) * mm, v(-7.75, -5.63) * mm, v(-7.8, -6.53) * mm]});
            skFitSpline(sketch, "E315", {"points": [v(-7.8, -6.53) * mm, v(-7.87, -7.98) * mm, v(-8.87, -8.66) * mm, v(-10.2, -8.17) * mm]});
            skFitSpline(sketch, "E316", {"points": [v(-10.2, -8.17) * mm, v(-10.5, -8.06) * mm, v(-10.77, -7.92) * mm, v(-11.11, -7.77) * mm]});
            skFitSpline(sketch, "E317", {"points": [v(-11.11, -7.77) * mm, v(-10.83, -8.76) * mm, v(-10.4, -9.55) * mm, v(-9.6, -10.14) * mm]});
            skFitSpline(sketch, "E318", {"points": [v(-9.6, -10.14) * mm, v(-8.24, -11.18) * mm, v(-6.68, -11.65) * mm, v(-5.02, -11.86) * mm]});
            skFitSpline(sketch, "E319", {"points": [v(-5.02, -11.86) * mm, v(-3.36, -12.08) * mm, v(-1.69, -12.11) * mm, v(-0.02, -12.17) * mm]});
            skFitSpline(sketch, "E320", {"points": [v(-0.02, -12.17) * mm, v(1.77, -12.22) * mm, v(3.54, -12.5) * mm, v(5.32, -12.72) * mm]});
            skFitSpline(sketch, "E321", {"points": [v(5.32, -12.72) * mm, v(8.35, -13.1) * mm, v(11.34, -13.75) * mm, v(14.36, -14.21) * mm]});
            skFitSpline(sketch, "E322", {"points": [v(14.36, -14.21) * mm, v(15.18, -14.34) * mm, v(15.97, -14.63) * mm, v(16.8, -14.73) * mm]});
            skFitSpline(sketch, "E323", {"points": [v(16.8, -14.73) * mm, v(16.9, -14.75) * mm, v(17.02, -14.82) * mm, v(17.01, -14.63) * mm]});
            skFitSpline(sketch, "E324", {"points": [v(17.01, -14.63) * mm, v(12.02, -12.4) * mm, v(7.75, -9.18) * mm, v(4.03, -5.13) * mm]});
            skFitSpline(sketch, "E325", {"points": [v(4.03, -5.13) * mm, v(2.16, -3.09) * mm, v(0.67, -0.8) * mm, v(-0.78, 1.53) * mm]});
            skFitSpline(sketch, "E326", {"points": [v(-0.78, 1.53) * mm, v(-4.46, 7.42) * mm, v(-6.77, 13.86) * mm, v(-8.17, 20.65) * mm]});
            skFitSpline(sketch, "E327", {"points": [v(-8.17, 20.65) * mm, v(-8.35, 21.53) * mm, v(-8.42, 22.43) * mm, v(-8.82, 23.24) * mm]});
            skFitSpline(sketch, "E328", {"points": [v(-8.82, 23.24) * mm, v(-9.7, 25.03) * mm, v(-11.2, 25.93) * mm, v(-13, 26.38) * mm]});
            skFitSpline(sketch, "E329", {"points": [v(-13, 26.38) * mm, v(-13.23, 26.44) * mm, v(-13.46, 26.48) * mm, v(-13.7, 26.5) * mm]});
            skFitSpline(sketch, "E330", {"points": [v(-13.7, 26.5) * mm, v(-14.73, 26.63) * mm, v(-15.75, 26.77) * mm, v(-16.72, 27.26) * mm]});
            skFitSpline(sketch, "E331", {"points": [v(-16.72, 27.26) * mm, v(-16.76, 26.85) * mm, v(-16.57, 26.54) * mm, v(-16.48, 26.2) * mm]});
            skFitSpline(sketch, "E332", {"points": [v(-16.48, 26.2) * mm, v(-16, 24.4) * mm, v(-15.74, 22.58) * mm, v(-16, 20.73) * mm]});
            skFitSpline(sketch, "E333", {"points": [v(-16, 20.73) * mm, v(-16.34, 18.26) * mm, v(-17.79, 16.82) * mm, v(-20.15, 16.25) * mm]});
            skFitSpline(sketch, "E334", {"points": [v(-20.15, 16.25) * mm, v(-23.4, 15.45) * mm, v(-26.44, 16.11) * mm, v(-29.3, 17.73) * mm]});
            skFitSpline(sketch, "E335", {"points": [v(-29.3, 17.73) * mm, v(-32.8, 19.7) * mm, v(-35.18, 22.74) * mm, v(-36.93, 26.32) * mm]});
            skFitSpline(sketch, "E336", {"points": [v(-36.93, 26.32) * mm, v(-38.65, 29.84) * mm, v(-39.63, 33.57) * mm, v(-39.2, 37.5) * mm]});
            skFitSpline(sketch, "E337", {"points": [v(-39.2, 37.5) * mm, v(-38.63, 42.7) * mm, v(-36.87, 47.38) * mm, v(-32.6, 50.7) * mm]});
            skFitSpline(sketch, "E338", {"points": [v(-32.6, 50.7) * mm, v(-31, 51.94) * mm, v(-29.21, 52.95) * mm, v(-27.17, 53.25) * mm]});
            skFitSpline(sketch, "E339", {"points": [v(-27.17, 53.25) * mm, v(-24.16, 53.7) * mm, v(-21.31, 53.26) * mm, v(-18.96, 51.14) * mm]});
            skFitSpline(sketch, "E340", {"points": [v(-18.96, 51.14) * mm, v(-17.44, 49.76) * mm, v(-17.08, 47.92) * mm, v(-17.36, 45.94) * mm]});
            skFitSpline(sketch, "E341", {"points": [v(-17.36, 45.94) * mm, v(-17.41, 45.6) * mm, v(-17.63, 45.32) * mm, v(-17.87, 45.07) * mm]});
            skFitSpline(sketch, "E342", {"points": [v(-17.87, 45.07) * mm, v(-18.18, 44.74) * mm, v(-18.5, 44.41) * mm, v(-18.82, 44.07) * mm]});
            skFitSpline(sketch, "E343", {"points": [v(-18.82, 44.07) * mm, v(-17.8, 43.58) * mm, v(-17.01, 42.78) * mm, v(-16.24, 41.96) * mm]});
            skFitSpline(sketch, "E344", {"points": [v(-16.24, 41.96) * mm, v(-15.3, 40.97) * mm, v(-14.34, 40.01) * mm, v(-13.2, 39.25) * mm]});
            skFitSpline(sketch, "E345", {"points": [v(-13.2, 39.25) * mm, v(-12.69, 38.9) * mm, v(-12.15, 38.94) * mm, v(-11.61, 38.96) * mm]});
            skFitSpline(sketch, "E346", {"points": [v(-11.61, 38.96) * mm, v(-11.36, 38.97) * mm, v(-11.24, 39.24) * mm, v(-11.12, 39.43) * mm]});
            skFitSpline(sketch, "E347", {"points": [v(-11.12, 39.43) * mm, v(-10.82, 39.9) * mm, v(-10.67, 40.43) * mm, v(-10.62, 40.96) * mm]});
            skFitSpline(sketch, "E348", {"points": [v(-10.62, 40.96) * mm, v(-10.29, 44.25) * mm, v(-10.66, 47.45) * mm, v(-11.87, 50.53) * mm]});
            skFitSpline(sketch, "E349", {"points": [v(-11.87, 50.53) * mm, v(-12.63, 52.45) * mm, v(-13.6, 54.26) * mm, v(-15, 55.8) * mm]});
            skFitSpline(sketch, "E350", {"points": [v(-15, 55.8) * mm, v(-16.53, 57.5) * mm, v(-18.38, 58.65) * mm, v(-20.61, 59.1) * mm]});
            skFitSpline(sketch, "E351", {"points": [v(-20.61, 59.1) * mm, v(-26.57, 60.31) * mm, v(-31.67, 58.5) * mm, v(-36.12, 54.5) * mm]});
            skFitSpline(sketch, "E352", {"points": [v(-36.12, 54.5) * mm, v(-38.56, 52.3) * mm, v(-39.83, 49.38) * mm, v(-40.94, 46.37) * mm]});
            skFitSpline(sketch, "E353", {"points": [v(-40.94, 46.37) * mm, v(-41.85, 43.9) * mm, v(-42.33, 41.33) * mm, v(-42.66, 38.73) * mm]});
            skFitSpline(sketch, "E354", {"points": [v(-42.66, 38.73) * mm, v(-42.7, 38.46) * mm, v(-42.67, 38.17) * mm, v(-42.85, 37.93) * mm]});
            skFitSpline(sketch, "E355", {"points": [v(-42.85, 36.81) * mm, v(-42.77, 36.37) * mm, v(-42.77, 35.93) * mm, v(-42.85, 35.49) * mm]});
            skFitSpline(sketch, "E356", {"points": [v(-42.85, 34.98) * mm, v(-42.8, 34.91) * mm, v(-42.8, 34.84) * mm, v(-42.85, 34.78) * mm]});
            skFitSpline(sketch, "E357", {"points": [v(40.63, -16.62) * mm, v(40.03, -16.65) * mm, v(39.42, -16.48) * mm, v(38.83, -16.7) * mm]});
            skFitSpline(sketch, "E358", {"points": [v(-42.85, 35.49) * mm, v(-42.69, 35.93) * mm, v(-42.69, 36.37) * mm, v(-42.85, 36.81) * mm]});
            skFitSpline(sketch, "E359", {"points": [v(-14.22, 61.96) * mm, v(-13.88, 61.8) * mm, v(-13.55, 61.8) * mm, v(-13.21, 61.96) * mm]});
            skFitSpline(sketch, "E360", {"points": [v(-42.85, 34.77) * mm, v(-42.7, 34.84) * mm, v(-42.72, 34.91) * mm, v(-42.85, 34.98) * mm]});
            skFitSpline(sketch, "E361", {"points": [v(36.2, -31.09) * mm, v(36.2, -31.19) * mm, v(36.14, -31.33) * mm, v(36.03, -31.52) * mm]});
            skFitSpline(sketch, "E362", {"points": [v(35.01, -30.98) * mm, v(34.51, -30.8) * mm, v(33.97, -30.7) * mm, v(33.37, -30.7) * mm]});
            skFitSpline(sketch, "E363", {"points": [v(27.52, -30.26) * mm, v(27.27, -29.84) * mm, v(27.06, -29.54) * mm, v(26.88, -29.35) * mm]});
            skFitSpline(sketch, "E364", {"points": [v(26.9, -29.28) * mm, v(26.91, -29.26) * mm, v(26.95, -29.22) * mm, v(27.02, -29.17) * mm]});
            skFitSpline(sketch, "E365", {"points": [v(27.02, -29.17) * mm, v(27.1, -29.12) * mm, v(27.16, -29.1) * mm, v(27.2, -29.1) * mm]});
            skFitSpline(sketch, "E366", {"points": [v(27.2, -29.1) * mm, v(27.32, -29.1) * mm, v(27.44, -29.17) * mm, v(27.55, -29.3) * mm]});
            skFitSpline(sketch, "E367", {"points": [v(27.55, -29.3) * mm, v(27.67, -29.44) * mm, v(27.78, -29.53) * mm, v(27.9, -29.57) * mm]});
            skFitSpline(sketch, "E368", {"points": [v(27.9, -29.57) * mm, v(28.63, -29.7) * mm, v(29.44, -29.76) * mm, v(30.32, -29.76) * mm]});
            skFitSpline(sketch, "E369", {"points": [v(34.41, -29.76) * mm, v(34.56, -29.76) * mm, v(34.8, -29.83) * mm, v(35.12, -29.97) * mm]});
            skFitSpline(sketch, "E370", {"points": [v(35.12, -29.97) * mm, v(35.46, -30.15) * mm, v(35.73, -30.31) * mm, v(35.93, -30.47) * mm]});
            skFitSpline(sketch, "E371", {"points": [v(35.93, -30.47) * mm, v(36.1, -30.6) * mm, v(36.2, -30.81) * mm, v(36.2, -31.09) * mm]});
            skFitSpline(sketch, "E372", {"points": [v(37.7, -29.32) * mm, v(38.17, -28.53) * mm, v(38.41, -27.65) * mm, v(38.41, -26.7) * mm]});
            skFitSpline(sketch, "E373", {"points": [v(38.41, -26.7) * mm, v(38.41, -26.04) * mm, v(38.22, -25.5) * mm, v(37.83, -25.09) * mm]});
            skFitSpline(sketch, "E374", {"points": [v(37.83, -25.09) * mm, v(37.44, -24.67) * mm, v(36.94, -24.4) * mm, v(36.33, -24.26) * mm]});
            skFitSpline(sketch, "E375", {"points": [v(36.33, -24.26) * mm, v(35.71, -24.13) * mm, v(34.95, -24.06) * mm, v(34.05, -24.06) * mm]});
            skFitSpline(sketch, "E376", {"points": [v(29.36, -24.3) * mm, v(28.94, -24.3) * mm, v(28.54, -24.31) * mm, v(28.15, -24.33) * mm]});
            skFitSpline(sketch, "E377", {"points": [v(28.15, -24.33) * mm, v(27.77, -24.35) * mm, v(27.48, -24.37) * mm, v(27.3, -24.39) * mm]});
            skFitSpline(sketch, "E378", {"points": [v(27.09, -23.13) * mm, v(28, -23.03) * mm, v(28.78, -22.97) * mm, v(29.45, -22.97) * mm]});
            skFitSpline(sketch, "E379", {"points": [v(36.14, -22.66) * mm, v(37.23, -22.66) * mm, v(38, -22.85) * mm, v(38.45, -23.23) * mm]});
            skFitSpline(sketch, "E380", {"points": [v(38.45, -23.23) * mm, v(38.93, -23.57) * mm, v(39.17, -24.28) * mm, v(39.17, -25.34) * mm]});
            skFitSpline(sketch, "E381", {"points": [v(39.17, -25.34) * mm, v(39.17, -26.27) * mm, v(39.07, -27.09) * mm, v(38.87, -27.8) * mm]});
            skFitSpline(sketch, "E382", {"points": [v(38.87, -27.8) * mm, v(38.67, -28.5) * mm, v(38.4, -29.07) * mm, v(38.04, -29.5) * mm]});
            skFitSpline(sketch, "E383", {"points": [v(41.6, -35.22) * mm, v(41.97, -35.64) * mm, v(42.27, -36.2) * mm, v(42.5, -36.9) * mm]});
            skFitSpline(sketch, "E384", {"points": [v(42.5, -36.9) * mm, v(42.74, -37.59) * mm, v(42.85, -38.1) * mm, v(42.85, -38.46) * mm]});
            skFitSpline(sketch, "E385", {"points": [v(42.85, -38.46) * mm, v(42.85, -39.3) * mm, v(42.5, -39.99) * mm, v(41.78, -40.53) * mm]});
            skFitSpline(sketch, "E386", {"points": [v(41.78, -40.53) * mm, v(41.06, -41.07) * mm, v(40, -41.34) * mm, v(38.6, -41.34) * mm]});
            skFitSpline(sketch, "E387", {"points": [v(38.6, -41.34) * mm, v(38.15, -41.34) * mm, v(37.7, -41.28) * mm, v(37.25, -41.15) * mm]});
            skFitSpline(sketch, "E388", {"points": [v(37.25, -41.15) * mm, v(36.8, -41.02) * mm, v(36.23, -40.79) * mm, v(35.56, -40.46) * mm]});
            skFitSpline(sketch, "E389", {"points": [v(35.56, -40.46) * mm, v(34.89, -40.13) * mm, v(34.18, -39.58) * mm, v(33.43, -38.82) * mm]});
            skFitSpline(sketch, "E390", {"points": [v(33.43, -38.82) * mm, v(32.68, -38.05) * mm, v(32.09, -37.3) * mm, v(31.65, -36.54) * mm]});
            skFitSpline(sketch, "E391", {"points": [v(31.65, -36.54) * mm, v(31.22, -35.8) * mm, v(30.9, -34.88) * mm, v(30.71, -33.8) * mm]});
            skFitSpline(sketch, "E392", {"points": [v(30.71, -33.8) * mm, v(30.52, -32.72) * mm, v(30.36, -31.52) * mm, v(30.25, -30.2) * mm]});
            skFitSpline(sketch, "E393", {"points": [v(29.88, -26.54) * mm, v(29.74, -25.38) * mm, v(29.63, -24.72) * mm, v(29.55, -24.56) * mm]});
            skFitSpline(sketch, "E394", {"points": [v(29.3, -24.3) * mm, v(29.2, -24.2) * mm, v(29.15, -24.15) * mm, v(29.13, -24.1) * mm]});
            skFitSpline(sketch, "E395", {"points": [v(29.13, -24.1) * mm, v(29.11, -24.07) * mm, v(29.1, -24.04) * mm, v(29.08, -24) * mm]});
            skFitSpline(sketch, "E396", {"points": [v(29.08, -24) * mm, v(29.12, -23.98) * mm, v(29.15, -23.96) * mm, v(29.18, -23.96) * mm]});
            skFitSpline(sketch, "E397", {"points": [v(29.55, -24.04) * mm, v(30.22, -24.23) * mm, v(30.7, -24.7) * mm, v(31.01, -25.46) * mm]});
            skFitSpline(sketch, "E398", {"points": [v(31.01, -25.46) * mm, v(31.32, -26.2) * mm, v(31.52, -26.85) * mm, v(31.61, -27.39) * mm]});
            skFitSpline(sketch, "E399", {"points": [v(31.61, -27.39) * mm, v(31.71, -27.92) * mm, v(31.76, -28.48) * mm, v(31.76, -29.06) * mm]});
            skFitSpline(sketch, "E400", {"points": [v(31.88, -31.82) * mm, v(31.88, -32.1) * mm, v(31.89, -32.36) * mm, v(31.92, -32.58) * mm]});
            skFitSpline(sketch, "E401", {"points": [v(31.92, -32.58) * mm, v(31.94, -32.8) * mm, v(32, -33.16) * mm, v(32.07, -33.64) * mm]});
            skFitSpline(sketch, "E402", {"points": [v(32.07, -33.64) * mm, v(32.15, -34.3) * mm, v(32.27, -34.99) * mm, v(32.45, -35.7) * mm]});
            skFitSpline(sketch, "E403", {"points": [v(32.45, -35.7) * mm, v(32.62, -36.42) * mm, v(32.86, -37.03) * mm, v(33.17, -37.52) * mm]});
            skFitSpline(sketch, "E404", {"points": [v(33.17, -37.52) * mm, v(33.47, -38.01) * mm, v(33.84, -38.43) * mm, v(34.26, -38.78) * mm]});
            skFitSpline(sketch, "E405", {"points": [v(34.26, -38.78) * mm, v(34.69, -39.09) * mm, v(35.16, -39.32) * mm, v(35.68, -39.48) * mm]});
            skFitSpline(sketch, "E406", {"points": [v(35.68, -39.48) * mm, v(36.2, -39.63) * mm, v(36.72, -39.71) * mm, v(37.27, -39.71) * mm]});
            skFitSpline(sketch, "E407", {"points": [v(38.3, -39.63) * mm, v(38.88, -39.54) * mm, v(39.37, -39.44) * mm, v(39.78, -39.32) * mm]});
            skFitSpline(sketch, "E408", {"points": [v(39.78, -39.32) * mm, v(40.19, -39.2) * mm, v(40.56, -39.06) * mm, v(40.88, -38.89) * mm]});
            skFitSpline(sketch, "E409", {"points": [v(40.88, -38.89) * mm, v(41.21, -38.72) * mm, v(41.47, -38.5) * mm, v(41.65, -38.22) * mm]});
            skFitSpline(sketch, "E410", {"points": [v(41.65, -38.22) * mm, v(41.83, -37.95) * mm, v(41.92, -37.64) * mm, v(41.92, -37.28) * mm]});
            skFitSpline(sketch, "E411", {"points": [v(41.92, -37.28) * mm, v(41.92, -37.03) * mm, v(41.88, -36.79) * mm, v(41.8, -36.55) * mm]});
            skFitSpline(sketch, "E412", {"points": [v(41.8, -36.55) * mm, v(41.73, -36.31) * mm, v(41.63, -36.11) * mm, v(41.52, -35.94) * mm]});
            skFitSpline(sketch, "E413", {"points": [v(41.52, -35.94) * mm, v(41.46, -35.83) * mm, v(41.42, -35.74) * mm, v(41.37, -35.68) * mm]});
            skFitSpline(sketch, "E414", {"points": [v(41.37, -35.68) * mm, v(41.32, -35.62) * mm, v(41.25, -35.53) * mm, v(41.15, -35.4) * mm]});
            skFitSpline(sketch, "E415", {"points": [v(40.72, -34.76) * mm, v(40.72, -34.65) * mm, v(40.78, -34.6) * mm, v(40.91, -34.6) * mm]});
            skFitSpline(sketch, "E416", {"points": [v(40.91, -34.6) * mm, v(41, -34.6) * mm, v(41.23, -34.8) * mm, v(41.6, -35.22) * mm]});
            skFitSpline(sketch, "E417", {"points": [v(24.15, -33.75) * mm, v(24.06, -33.18) * mm, v(23.87, -31.77) * mm, v(23.56, -29.53) * mm]});
            skFitSpline(sketch, "E418", {"points": [v(23.5, -28.89) * mm, v(23.5, -28.54) * mm, v(23.58, -28.37) * mm, v(23.75, -28.37) * mm]});
            skFitSpline(sketch, "E419", {"points": [v(23.75, -28.37) * mm, v(23.88, -28.37) * mm, v(24.04, -28.42) * mm, v(24.23, -28.54) * mm]});
            skFitSpline(sketch, "E420", {"points": [v(26.33, -30.01) * mm, v(26.43, -30.09) * mm, v(26.48, -30.19) * mm, v(26.48, -30.3) * mm]});
            skFitSpline(sketch, "E421", {"points": [v(26.17, -30.3) * mm, v(26.07, -30.28) * mm, v(25.91, -30.2) * mm, v(25.7, -30.04) * mm]});
            skFitSpline(sketch, "E422", {"points": [v(25.7, -30.04) * mm, v(25.49, -29.9) * mm, v(25.34, -29.82) * mm, v(25.26, -29.82) * mm]});
            skFitSpline(sketch, "E423", {"points": [v(25.26, -29.82) * mm, v(25.19, -29.82) * mm, v(25.15, -29.98) * mm, v(25.15, -30.3) * mm]});
            skFitSpline(sketch, "E424", {"points": [v(25.79, -35.64) * mm, v(25.8, -35.72) * mm, v(25.82, -35.8) * mm, v(25.83, -35.86) * mm]});
            skFitSpline(sketch, "E425", {"points": [v(25.83, -35.86) * mm, v(25.85, -35.93) * mm, v(25.87, -35.98) * mm, v(25.88, -36) * mm]});
            skFitSpline(sketch, "E426", {"points": [v(24.4, -35.44) * mm, v(24.32, -34.88) * mm, v(24.23, -34.32) * mm, v(24.15, -33.75) * mm]});
            skFitSpline(sketch, "E427", {"points": [v(21.46, -30.67) * mm, v(20.87, -29.75) * mm, v(20.57, -29.17) * mm, v(20.57, -28.93) * mm]});
            skFitSpline(sketch, "E428", {"points": [v(20.57, -28.93) * mm, v(20.57, -28.55) * mm, v(20.73, -28.37) * mm, v(21.05, -28.37) * mm]});
            skFitSpline(sketch, "E429", {"points": [v(21.05, -28.37) * mm, v(21.3, -28.37) * mm, v(21.63, -28.5) * mm, v(22.03, -28.76) * mm]});
            skFitSpline(sketch, "E430", {"points": [v(22.03, -28.76) * mm, v(22.44, -29.03) * mm, v(22.83, -29.4) * mm, v(23.19, -29.85) * mm]});
            skFitSpline(sketch, "E431", {"points": [v(23.89, -30.75) * mm, v(24.12, -30.85) * mm, v(24.23, -31.02) * mm, v(24.23, -31.25) * mm]});
            skFitSpline(sketch, "E432", {"points": [v(24.23, -31.25) * mm, v(24.23, -31.3) * mm, v(24.2, -31.35) * mm, v(24.14, -31.4) * mm]});
            skFitSpline(sketch, "E433", {"points": [v(24.14, -31.4) * mm, v(24.03, -31.4) * mm, v(23.87, -31.33) * mm, v(23.65, -31.18) * mm]});
            skFitSpline(sketch, "E434", {"points": [v(23.19, -30.77) * mm, v(22.74, -30.3) * mm, v(22.42, -30.07) * mm, v(22.24, -30.07) * mm]});
            skFitSpline(sketch, "E435", {"points": [v(22.24, -30.07) * mm, v(22.15, -30.07) * mm, v(22.1, -30.14) * mm, v(22.1, -30.27) * mm]});
            skFitSpline(sketch, "E436", {"points": [v(22.1, -30.27) * mm, v(22.1, -30.43) * mm, v(22.16, -30.68) * mm, v(22.27, -31) * mm]});
            skFitSpline(sketch, "E437", {"points": [v(22.27, -31) * mm, v(22.38, -31.33) * mm, v(22.44, -31.56) * mm, v(22.47, -31.7) * mm]});
            skFitSpline(sketch, "E438", {"points": [v(22.47, -31.7) * mm, v(22.5, -31.84) * mm, v(22.52, -31.96) * mm, v(22.53, -32.05) * mm]});
            skFitSpline(sketch, "E439", {"points": [v(22.53, -32.05) * mm, v(22.41, -32.05) * mm, v(22.06, -31.59) * mm, v(21.46, -30.67) * mm]});
            skFitSpline(sketch, "E440", {"points": [v(15.02, -29.33) * mm, v(14.92, -29.28) * mm, v(14.83, -29.19) * mm, v(14.76, -29.06) * mm]});
            skFitSpline(sketch, "E441", {"points": [v(14.76, -29.06) * mm, v(14.7, -28.94) * mm, v(14.65, -28.82) * mm, v(14.65, -28.72) * mm]});
            skFitSpline(sketch, "E442", {"points": [v(14.65, -28.72) * mm, v(14.65, -28.52) * mm, v(14.85, -28.42) * mm, v(15.24, -28.42) * mm]});
            skFitSpline(sketch, "E443", {"points": [v(16.71, -28.55) * mm, v(17.06, -28.55) * mm, v(17.39, -28.64) * mm, v(17.7, -28.8) * mm]});
            skFitSpline(sketch, "E444", {"points": [v(17.7, -28.8) * mm, v(18, -28.96) * mm, v(18.35, -29.24) * mm, v(18.73, -29.65) * mm]});
            skFitSpline(sketch, "E445", {"points": [v(18.73, -29.65) * mm, v(19.1, -30.06) * mm, v(19.4, -30.54) * mm, v(19.6, -31.09) * mm]});
            skFitSpline(sketch, "E446", {"points": [v(19.6, -31.09) * mm, v(19.8, -31.63) * mm, v(19.96, -32.08) * mm, v(20.05, -32.43) * mm]});
            skFitSpline(sketch, "E447", {"points": [v(20.05, -32.43) * mm, v(20.14, -32.78) * mm, v(20.2, -33.1) * mm, v(20.25, -33.38) * mm]});
            skFitSpline(sketch, "E448", {"points": [v(20.25, -33.38) * mm, v(20.3, -33.67) * mm, v(20.32, -33.9) * mm, v(20.34, -34.1) * mm]});
            skFitSpline(sketch, "E449", {"points": [v(20.34, -34.1) * mm, v(20.35, -34.28) * mm, v(20.36, -34.42) * mm, v(20.36, -34.5) * mm]});
            skFitSpline(sketch, "E450", {"points": [v(20.36, -34.5) * mm, v(20.36, -35.53) * mm, v(20.07, -36.04) * mm, v(19.5, -36.04) * mm]});
            skFitSpline(sketch, "E451", {"points": [v(19.5, -36.04) * mm, v(18.97, -36.04) * mm, v(18.24, -35.55) * mm, v(17.3, -34.56) * mm]});
            skFitSpline(sketch, "E452", {"points": [v(16.63, -33.84) * mm, v(16.43, -33.63) * mm, v(16.26, -33.42) * mm, v(16.13, -33.2) * mm]});
            skFitSpline(sketch, "E453", {"points": [v(16.13, -33.2) * mm, v(16, -32.97) * mm, v(15.93, -32.75) * mm, v(15.93, -32.53) * mm]});
            skFitSpline(sketch, "E454", {"points": [v(15.93, -32.53) * mm, v(15.93, -32.47) * mm, v(15.96, -32.39) * mm, v(16.01, -32.3) * mm]});
            skFitSpline(sketch, "E455", {"points": [v(16.46, -32.84) * mm, v(16.73, -33.22) * mm, v(17.05, -33.61) * mm, v(17.43, -34) * mm]});
            skFitSpline(sketch, "E456", {"points": [v(17.43, -34) * mm, v(17.8, -34.4) * mm, v(18.13, -34.6) * mm, v(18.4, -34.6) * mm]});
            skFitSpline(sketch, "E457", {"points": [v(18.4, -34.6) * mm, v(18.72, -34.6) * mm, v(18.88, -34.26) * mm, v(18.88, -33.58) * mm]});
            skFitSpline(sketch, "E458", {"points": [v(18.88, -33.58) * mm, v(18.88, -33.1) * mm, v(18.81, -32.5) * mm, v(18.68, -31.8) * mm]});
            skFitSpline(sketch, "E459", {"points": [v(18.68, -31.8) * mm, v(18.54, -31.1) * mm, v(18.39, -30.58) * mm, v(18.21, -30.24) * mm]});
            skFitSpline(sketch, "E460", {"points": [v(18.21, -30.24) * mm, v(18.04, -29.9) * mm, v(17.85, -29.68) * mm, v(17.65, -29.57) * mm]});
            skFitSpline(sketch, "E461", {"points": [v(17.65, -29.57) * mm, v(17.45, -29.46) * mm, v(17.22, -29.4) * mm, v(16.96, -29.4) * mm]});
            skFitSpline(sketch, "E462", {"points": [v(14.54, -29.14) * mm, v(14.54, -28.69) * mm, v(14.68, -28.46) * mm, v(14.97, -28.46) * mm]});
            skFitSpline(sketch, "E463", {"points": [v(14.97, -28.46) * mm, v(15.12, -28.46) * mm, v(15.3, -28.55) * mm, v(15.53, -28.73) * mm]});
            skFitSpline(sketch, "E464", {"points": [v(15.53, -28.73) * mm, v(15.72, -28.93) * mm, v(15.88, -29.18) * mm, v(16, -29.48) * mm]});
            skFitSpline(sketch, "E465", {"points": [v(16, -29.48) * mm, v(16.12, -29.78) * mm, v(16.2, -30.05) * mm, v(16.26, -30.28) * mm]});
            skFitSpline(sketch, "E466", {"points": [v(16.26, -30.28) * mm, v(16.31, -30.5) * mm, v(16.35, -30.78) * mm, v(16.38, -31.1) * mm]});
            skFitSpline(sketch, "E467", {"points": [v(16.85, -35.3) * mm, v(16.85, -35.79) * mm, v(16.74, -36.03) * mm, v(16.52, -36.03) * mm]});
            skFitSpline(sketch, "E468", {"points": [v(16.52, -36.03) * mm, v(16.3, -36.03) * mm, v(16.02, -35.88) * mm, v(15.66, -35.6) * mm]});
            skFitSpline(sketch, "E469", {"points": [v(15.66, -35.6) * mm, v(15.3, -35.35) * mm, v(14.71, -34.87) * mm, v(13.9, -34.14) * mm]});
            skFitSpline(sketch, "E470", {"points": [v(13.9, -34.14) * mm, v(13.85, -34.08) * mm, v(13.8, -34.03) * mm, v(13.78, -33.99) * mm]});
            skFitSpline(sketch, "E471", {"points": [v(13.78, -33.99) * mm, v(13.76, -33.95) * mm, v(13.74, -33.91) * mm, v(13.72, -33.87) * mm]});
            skFitSpline(sketch, "E472", {"points": [v(13.72, -33.87) * mm, v(13.72, -33.85) * mm, v(13.76, -33.81) * mm, v(13.82, -33.78) * mm]});
            skFitSpline(sketch, "E473", {"points": [v(13.82, -33.78) * mm, v(13.91, -33.78) * mm, v(14.02, -33.82) * mm, v(14.16, -33.91) * mm]});
            skFitSpline(sketch, "E474", {"points": [v(14.16, -33.91) * mm, v(14.3, -34) * mm, v(14.42, -34.1) * mm, v(14.54, -34.18) * mm]});
            skFitSpline(sketch, "E475", {"points": [v(14.54, -34.18) * mm, v(14.65, -34.27) * mm, v(14.76, -34.36) * mm, v(14.85, -34.45) * mm]});
            skFitSpline(sketch, "E476", {"points": [v(15.26, -34.75) * mm, v(15.27, -34.73) * mm, v(15.28, -34.71) * mm, v(15.3, -34.68) * mm]});
            skFitSpline(sketch, "E477", {"points": [v(15.3, -34.68) * mm, v(15.32, -34.65) * mm, v(15.33, -34.6) * mm, v(15.33, -34.51) * mm]});
            skFitSpline(sketch, "E478", {"points": [v(8.27, -29.31) * mm, v(8.17, -29.25) * mm, v(8.1, -29.17) * mm, v(8.04, -29.08) * mm]});
            skFitSpline(sketch, "E479", {"points": [v(7.89, -28.74) * mm, v(7.89, -28.55) * mm, v(8.08, -28.46) * mm, v(8.47, -28.35) * mm]});
            skFitSpline(sketch, "E480", {"points": [v(10.14, -28.6) * mm, v(10.8, -28.66) * mm, v(11.4, -28.9) * mm, v(11.9, -29.32) * mm]});
            skFitSpline(sketch, "E481", {"points": [v(11.9, -29.32) * mm, v(12.39, -29.73) * mm, v(12.8, -30.26) * mm, v(13.12, -30.9) * mm]});
            skFitSpline(sketch, "E482", {"points": [v(13.12, -30.9) * mm, v(13.45, -31.53) * mm, v(13.66, -32.18) * mm, v(13.76, -32.84) * mm]});
            skFitSpline(sketch, "E483", {"points": [v(13.76, -32.84) * mm, v(13.87, -33.5) * mm, v(13.92, -34.06) * mm, v(13.92, -34.53) * mm]});
            skFitSpline(sketch, "E484", {"points": [v(13.92, -34.53) * mm, v(13.92, -35.58) * mm, v(13.67, -36.1) * mm, v(13.16, -36.1) * mm]});
            skFitSpline(sketch, "E485", {"points": [v(13.16, -36.1) * mm, v(12.73, -36.1) * mm, v(12.1, -35.65) * mm, v(11.28, -34.74) * mm]});
            skFitSpline(sketch, "E486", {"points": [v(10.47, -33.88) * mm, v(10.2, -33.6) * mm, v(10.01, -33.4) * mm, v(9.88, -33.26) * mm]});
            skFitSpline(sketch, "E487", {"points": [v(9.88, -33.26) * mm, v(9.75, -33.12) * mm, v(9.62, -32.94) * mm, v(9.49, -32.74) * mm]});
            skFitSpline(sketch, "E488", {"points": [v(9.49, -32.74) * mm, v(9.35, -32.54) * mm, v(9.28, -32.33) * mm, v(9.28, -32.1) * mm]});
            skFitSpline(sketch, "E489", {"points": [v(9.28, -32.1) * mm, v(9.28, -31.93) * mm, v(9.32, -31.84) * mm, v(9.4, -31.84) * mm]});
            skFitSpline(sketch, "E490", {"points": [v(9.4, -31.84) * mm, v(9.48, -31.84) * mm, v(9.57, -31.9) * mm, v(9.69, -32.05) * mm]});
            skFitSpline(sketch, "E491", {"points": [v(11.14, -33.94) * mm, v(11.65, -34.48) * mm, v(12.02, -34.75) * mm, v(12.27, -34.75) * mm]});
            skFitSpline(sketch, "E492", {"points": [v(12.27, -34.75) * mm, v(12.49, -34.75) * mm, v(12.6, -34.54) * mm, v(12.6, -34.13) * mm]});
            skFitSpline(sketch, "E493", {"points": [v(12.13, -31.6) * mm, v(12.02, -31.02) * mm, v(11.87, -30.55) * mm, v(11.68, -30.21) * mm]});
            skFitSpline(sketch, "E494", {"points": [v(11.68, -30.21) * mm, v(11.5, -29.87) * mm, v(11.29, -29.65) * mm, v(11.07, -29.55) * mm]});
            skFitSpline(sketch, "E495", {"points": [v(11.07, -29.55) * mm, v(10.85, -29.44) * mm, v(10.6, -29.4) * mm, v(10.33, -29.4) * mm]});
            skFitSpline(sketch, "E496", {"points": [v(8.7, -28.7) * mm, v(8.82, -28.7) * mm, v(8.99, -28.7) * mm, v(9.2, -28.7) * mm]});
            skFitSpline(sketch, "E497", {"points": [v(9.2, -28.7) * mm, v(9.37, -28.7) * mm, v(9.46, -28.75) * mm, v(9.46, -28.84) * mm]});
            skFitSpline(sketch, "E498", {"points": [v(10.47, -37.68) * mm, v(10.47, -38.03) * mm, v(10.49, -38.32) * mm, v(10.52, -38.56) * mm]});
            skFitSpline(sketch, "E499", {"points": [v(10.52, -38.56) * mm, v(10.56, -38.8) * mm, v(10.61, -39.05) * mm, v(10.68, -39.3) * mm]});
            skFitSpline(sketch, "E500", {"points": [v(10.68, -39.3) * mm, v(10.78, -39.59) * mm, v(10.95, -39.8) * mm, v(11.18, -39.95) * mm]});
            skFitSpline(sketch, "E501", {"points": [v(11.18, -39.95) * mm, v(11.44, -40.14) * mm, v(11.82, -40.24) * mm, v(12.3, -40.24) * mm]});
            skFitSpline(sketch, "E502", {"points": [v(12.3, -40.24) * mm, v(12.8, -40.24) * mm, v(13.23, -40.1) * mm, v(13.6, -39.8) * mm]});
            skFitSpline(sketch, "E503", {"points": [v(13.6, -39.8) * mm, v(13.97, -39.51) * mm, v(14.15, -39.17) * mm, v(14.15, -38.79) * mm]});
            skFitSpline(sketch, "E504", {"points": [v(14.15, -38.79) * mm, v(14.15, -38.63) * mm, v(14.09, -38.42) * mm, v(13.97, -38.16) * mm]});
            skFitSpline(sketch, "E505", {"points": [v(13.97, -38.16) * mm, v(13.84, -37.9) * mm, v(13.64, -37.65) * mm, v(13.36, -37.43) * mm]});
            skFitSpline(sketch, "E506", {"points": [v(13.36, -37.43) * mm, v(13.09, -37.2) * mm, v(12.88, -37.06) * mm, v(12.75, -36.97) * mm]});
            skFitSpline(sketch, "E507", {"points": [v(12.75, -36.97) * mm, v(12.63, -36.89) * mm, v(12.46, -36.8) * mm, v(12.25, -36.7) * mm]});
            skFitSpline(sketch, "E508", {"points": [v(11.22, -36.28) * mm, v(11.05, -36.22) * mm, v(10.93, -36.17) * mm, v(10.85, -36.13) * mm]});
            skFitSpline(sketch, "E509", {"points": [v(10.85, -36.13) * mm, v(10.78, -36.1) * mm, v(10.71, -36.05) * mm, v(10.66, -36) * mm]});
            skFitSpline(sketch, "E510", {"points": [v(10.7, -35.94) * mm, v(10.92, -35.94) * mm, v(11.3, -36.06) * mm, v(11.84, -36.3) * mm]});
            skFitSpline(sketch, "E511", {"points": [v(11.84, -36.3) * mm, v(12.39, -36.55) * mm, v(12.92, -36.85) * mm, v(13.44, -37.22) * mm]});
            skFitSpline(sketch, "E512", {"points": [v(13.44, -37.22) * mm, v(13.97, -37.58) * mm, v(14.33, -37.93) * mm, v(14.53, -38.26) * mm]});
            skFitSpline(sketch, "E513", {"points": [v(14.53, -38.26) * mm, v(14.73, -38.6) * mm, v(14.83, -39.01) * mm, v(14.83, -39.5) * mm]});
            skFitSpline(sketch, "E514", {"points": [v(14.83, -39.5) * mm, v(14.83, -40) * mm, v(14.68, -40.42) * mm, v(14.4, -40.78) * mm]});
            skFitSpline(sketch, "E515", {"points": [v(14.4, -40.78) * mm, v(14.1, -41.15) * mm, v(13.7, -41.33) * mm, v(13.16, -41.33) * mm]});
            skFitSpline(sketch, "E516", {"points": [v(13.16, -41.33) * mm, v(12.49, -41.33) * mm, v(11.78, -41.05) * mm, v(11.02, -40.5) * mm]});
            skFitSpline(sketch, "E517", {"points": [v(11.02, -40.5) * mm, v(10.26, -39.94) * mm, v(9.75, -39.25) * mm, v(9.49, -38.43) * mm]});
            skFitSpline(sketch, "E518", {"points": [v(9.49, -38.43) * mm, v(9.22, -37.6) * mm, v(9.02, -36.56) * mm, v(8.88, -35.3) * mm]});
            skFitSpline(sketch, "E519", {"points": [v(8.5, -31.75) * mm, v(8.4, -30.62) * mm, v(8.24, -29.7) * mm, v(8.04, -28.95) * mm]});
            skFitSpline(sketch, "E520", {"points": [v(8.04, -28.95) * mm, v(8.04, -28.79) * mm, v(8.26, -28.7) * mm, v(8.7, -28.7) * mm]});
            skFitSpline(sketch, "E521", {"points": [v(2.67, -29.33) * mm, v(2.57, -29.28) * mm, v(2.48, -29.19) * mm, v(2.4, -29.06) * mm]});
            skFitSpline(sketch, "E522", {"points": [v(2.4, -29.06) * mm, v(2.34, -28.94) * mm, v(2.3, -28.82) * mm, v(2.3, -28.72) * mm]});
            skFitSpline(sketch, "E523", {"points": [v(2.3, -28.72) * mm, v(2.3, -28.52) * mm, v(2.5, -28.42) * mm, v(2.88, -28.42) * mm]});
            skFitSpline(sketch, "E524", {"points": [v(4.36, -28.55) * mm, v(4.7, -28.55) * mm, v(5.04, -28.64) * mm, v(5.35, -28.8) * mm]});
            skFitSpline(sketch, "E525", {"points": [v(5.35, -28.8) * mm, v(5.66, -28.96) * mm, v(6, -29.24) * mm, v(6.37, -29.65) * mm]});
            skFitSpline(sketch, "E526", {"points": [v(6.37, -29.65) * mm, v(6.75, -30.06) * mm, v(7.04, -30.54) * mm, v(7.25, -31.09) * mm]});
            skFitSpline(sketch, "E527", {"points": [v(7.25, -31.09) * mm, v(7.45, -31.63) * mm, v(7.6, -32.08) * mm, v(7.7, -32.43) * mm]});
            skFitSpline(sketch, "E528", {"points": [v(7.7, -32.43) * mm, v(7.78, -32.78) * mm, v(7.85, -33.1) * mm, v(7.9, -33.38) * mm]});
            skFitSpline(sketch, "E529", {"points": [v(7.9, -33.38) * mm, v(7.94, -33.67) * mm, v(7.97, -33.9) * mm, v(7.98, -34.1) * mm]});
            skFitSpline(sketch, "E530", {"points": [v(7.98, -34.1) * mm, v(8, -34.28) * mm, v(8, -34.42) * mm, v(8, -34.5) * mm]});
            skFitSpline(sketch, "E531", {"points": [v(8, -34.5) * mm, v(8, -35.53) * mm, v(7.72, -36.04) * mm, v(7.15, -36.04) * mm]});
            skFitSpline(sketch, "E532", {"points": [v(7.15, -36.04) * mm, v(6.62, -36.04) * mm, v(5.88, -35.55) * mm, v(4.94, -34.56) * mm]});
            skFitSpline(sketch, "E533", {"points": [v(4.28, -33.84) * mm, v(4.07, -33.63) * mm, v(3.9, -33.42) * mm, v(3.78, -33.2) * mm]});
            skFitSpline(sketch, "E534", {"points": [v(3.78, -33.2) * mm, v(3.65, -32.97) * mm, v(3.58, -32.75) * mm, v(3.58, -32.53) * mm]});
            skFitSpline(sketch, "E535", {"points": [v(3.58, -32.53) * mm, v(3.58, -32.47) * mm, v(3.6, -32.39) * mm, v(3.66, -32.3) * mm]});
            skFitSpline(sketch, "E536", {"points": [v(4.1, -32.84) * mm, v(4.38, -33.22) * mm, v(4.7, -33.61) * mm, v(5.07, -34) * mm]});
            skFitSpline(sketch, "E537", {"points": [v(5.07, -34) * mm, v(5.45, -34.4) * mm, v(5.77, -34.6) * mm, v(6.04, -34.6) * mm]});
            skFitSpline(sketch, "E538", {"points": [v(6.04, -34.6) * mm, v(6.37, -34.6) * mm, v(6.53, -34.26) * mm, v(6.53, -33.58) * mm]});
            skFitSpline(sketch, "E539", {"points": [v(6.53, -33.58) * mm, v(6.53, -33.1) * mm, v(6.46, -32.5) * mm, v(6.33, -31.8) * mm]});
            skFitSpline(sketch, "E540", {"points": [v(6.33, -31.8) * mm, v(6.19, -31.1) * mm, v(6.03, -30.58) * mm, v(5.86, -30.24) * mm]});
            skFitSpline(sketch, "E541", {"points": [v(5.86, -30.24) * mm, v(5.69, -29.9) * mm, v(5.5, -29.68) * mm, v(5.3, -29.57) * mm]});
            skFitSpline(sketch, "E542", {"points": [v(5.3, -29.57) * mm, v(5.1, -29.46) * mm, v(4.87, -29.4) * mm, v(4.6, -29.4) * mm]});
            skFitSpline(sketch, "E543", {"points": [v(2.19, -29.14) * mm, v(2.19, -28.69) * mm, v(2.33, -28.46) * mm, v(2.62, -28.46) * mm]});
            skFitSpline(sketch, "E544", {"points": [v(2.62, -28.46) * mm, v(2.77, -28.46) * mm, v(2.96, -28.55) * mm, v(3.17, -28.73) * mm]});
            skFitSpline(sketch, "E545", {"points": [v(3.17, -28.73) * mm, v(3.37, -28.93) * mm, v(3.52, -29.18) * mm, v(3.65, -29.48) * mm]});
            skFitSpline(sketch, "E546", {"points": [v(3.65, -29.48) * mm, v(3.77, -29.78) * mm, v(3.86, -30.05) * mm, v(3.9, -30.28) * mm]});
            skFitSpline(sketch, "E547", {"points": [v(3.9, -30.28) * mm, v(3.96, -30.5) * mm, v(4, -30.78) * mm, v(4.02, -31.1) * mm]});
            skFitSpline(sketch, "E548", {"points": [v(4.5, -35.3) * mm, v(4.5, -35.79) * mm, v(4.38, -36.03) * mm, v(4.16, -36.03) * mm]});
            skFitSpline(sketch, "E549", {"points": [v(4.16, -36.03) * mm, v(3.96, -36.03) * mm, v(3.67, -35.88) * mm, v(3.3, -35.6) * mm]});
            skFitSpline(sketch, "E550", {"points": [v(3.3, -35.6) * mm, v(2.95, -35.35) * mm, v(2.36, -34.87) * mm, v(1.54, -34.14) * mm]});
            skFitSpline(sketch, "E551", {"points": [v(1.54, -34.14) * mm, v(1.5, -34.08) * mm, v(1.45, -34.03) * mm, v(1.43, -33.99) * mm]});
            skFitSpline(sketch, "E552", {"points": [v(1.43, -33.99) * mm, v(1.4, -33.95) * mm, v(1.38, -33.91) * mm, v(1.37, -33.87) * mm]});
            skFitSpline(sketch, "E553", {"points": [v(1.37, -33.87) * mm, v(1.37, -33.85) * mm, v(1.4, -33.81) * mm, v(1.47, -33.78) * mm]});
            skFitSpline(sketch, "E554", {"points": [v(1.47, -33.78) * mm, v(1.56, -33.78) * mm, v(1.67, -33.82) * mm, v(1.8, -33.91) * mm]});
            skFitSpline(sketch, "E555", {"points": [v(1.8, -33.91) * mm, v(1.94, -34) * mm, v(2.07, -34.1) * mm, v(2.18, -34.18) * mm]});
            skFitSpline(sketch, "E556", {"points": [v(2.18, -34.18) * mm, v(2.3, -34.27) * mm, v(2.4, -34.36) * mm, v(2.5, -34.45) * mm]});
            skFitSpline(sketch, "E557", {"points": [v(2.9, -34.75) * mm, v(2.92, -34.73) * mm, v(2.93, -34.71) * mm, v(2.95, -34.68) * mm]});
            skFitSpline(sketch, "E558", {"points": [v(2.95, -34.68) * mm, v(2.97, -34.65) * mm, v(2.98, -34.6) * mm, v(2.98, -34.51) * mm]});
            skFitSpline(sketch, "E559", {"points": [v(0.84, -30.58) * mm, v(0.58, -30.28) * mm, v(0.36, -30.13) * mm, v(0.17, -30.13) * mm]});
            skFitSpline(sketch, "E560", {"points": [v(0.17, -30.13) * mm, v(0.01, -30.13) * mm, v(-0.07, -30.34) * mm, v(-0.07, -30.77) * mm]});
            skFitSpline(sketch, "E561", {"points": [v(0.85, -37.11) * mm, v(1.16, -38.88) * mm, v(1.31, -40.07) * mm, v(1.31, -40.66) * mm]});
            skFitSpline(sketch, "E562", {"points": [v(1.31, -40.66) * mm, v(1.31, -41.15) * mm, v(1.2, -41.4) * mm, v(0.96, -41.4) * mm]});
            skFitSpline(sketch, "E563", {"points": [v(0.32, -41.16) * mm, v(0.12, -41.06) * mm, v(-0.05, -40.98) * mm, v(-0.17, -40.93) * mm]});
            skFitSpline(sketch, "E564", {"points": [v(-0.17, -40.93) * mm, v(-0.3, -40.88) * mm, v(-0.44, -40.82) * mm, v(-0.6, -40.76) * mm]});
            skFitSpline(sketch, "E565", {"points": [v(-0.6, -40.76) * mm, v(-0.78, -40.7) * mm, v(-1.03, -40.66) * mm, v(-1.36, -40.66) * mm]});
            skFitSpline(sketch, "E566", {"points": [v(-1.36, -40.66) * mm, v(-1.61, -40.66) * mm, v(-1.73, -40.49) * mm, v(-1.73, -40.14) * mm]});
            skFitSpline(sketch, "E567", {"points": [v(-1.73, -40.14) * mm, v(-1.73, -39.9) * mm, v(-1.62, -39.79) * mm, v(-1.4, -39.79) * mm]});
            skFitSpline(sketch, "E568", {"points": [v(-1.4, -39.79) * mm, v(-1, -40.03) * mm, v(-0.75, -40.16) * mm, v(-0.65, -40.16) * mm]});
            skFitSpline(sketch, "E569", {"points": [v(-0.65, -40.16) * mm, v(-0.5, -40.16) * mm, v(-0.43, -40) * mm, v(-0.43, -39.67) * mm]});
            skFitSpline(sketch, "E570", {"points": [v(-1.62, -29.37) * mm, v(-1.62, -28.8) * mm, v(-1.5, -28.52) * mm, v(-1.25, -28.52) * mm]});
            skFitSpline(sketch, "E571", {"points": [v(-1.25, -28.52) * mm, v(-0.9, -28.52) * mm, v(-0.36, -28.87) * mm, v(0.38, -29.58) * mm]});
            skFitSpline(sketch, "E572", {"points": [v(0.38, -29.58) * mm, v(1.12, -30.28) * mm, v(1.49, -30.7) * mm, v(1.49, -30.85) * mm]});
            skFitSpline(sketch, "E573", {"points": [v(1.49, -30.85) * mm, v(1.49, -30.96) * mm, v(1.44, -31.02) * mm, v(1.35, -31.02) * mm]});
            skFitSpline(sketch, "E574", {"points": [v(1.35, -31.02) * mm, v(1.26, -31.02) * mm, v(1.09, -30.87) * mm, v(0.84, -30.58) * mm]});
            skFitSpline(sketch, "E575", {"points": [v(-0.94, -35.28) * mm, v(-0.83, -35.19) * mm, v(-0.72, -35.14) * mm, v(-0.6, -35.14) * mm]});
            skFitSpline(sketch, "E576", {"points": [v(-0.6, -35.14) * mm, v(-0.53, -35.15) * mm, v(-0.48, -35.19) * mm, v(-0.45, -35.24) * mm]});
            skFitSpline(sketch, "E577", {"points": [v(-0.45, -35.24) * mm, v(-0.43, -35.3) * mm, v(-0.41, -35.36) * mm, v(-0.41, -35.45) * mm]});
            skFitSpline(sketch, "E578", {"points": [v(-0.36, -35.65) * mm, v(-0.24, -35.85) * mm, v(-0.18, -36) * mm, v(-0.18, -36.1) * mm]});
            skFitSpline(sketch, "E579", {"points": [v(-2.27, -36.11) * mm, v(-3.28, -36.11) * mm, v(-3.98, -35.64) * mm, v(-4.35, -34.7) * mm]});
            skFitSpline(sketch, "E580", {"points": [v(-4.35, -34.7) * mm, v(-4.72, -33.76) * mm, v(-4.97, -32.87) * mm, v(-5.1, -32.03) * mm]});
            skFitSpline(sketch, "E581", {"points": [v(-5.1, -32.03) * mm, v(-5.24, -31.2) * mm, v(-5.3, -30.66) * mm, v(-5.32, -30.45) * mm]});
            skFitSpline(sketch, "E582", {"points": [v(-5.32, -30.45) * mm, v(-5.33, -30.24) * mm, v(-5.34, -30.04) * mm, v(-5.34, -29.84) * mm]});
            skFitSpline(sketch, "E583", {"points": [v(-5.34, -29.84) * mm, v(-5.34, -28.94) * mm, v(-5.11, -28.49) * mm, v(-4.66, -28.49) * mm]});
            skFitSpline(sketch, "E584", {"points": [v(-4.66, -28.49) * mm, v(-4.2, -28.49) * mm, v(-3.5, -29) * mm, v(-2.53, -30.03) * mm]});
            skFitSpline(sketch, "E585", {"points": [v(-1.85, -30.67) * mm, v(-1.51, -30.98) * mm, v(-1.27, -31.23) * mm, v(-1.13, -31.41) * mm]});
            skFitSpline(sketch, "E586", {"points": [v(-1.13, -31.41) * mm, v(-0.99, -31.6) * mm, v(-0.92, -31.79) * mm, v(-0.92, -32) * mm]});
            skFitSpline(sketch, "E587", {"points": [v(-0.92, -32) * mm, v(-0.92, -32.05) * mm, v(-0.95, -32.1) * mm, v(-1.02, -32.17) * mm]});
            skFitSpline(sketch, "E588", {"points": [v(-1.02, -32.17) * mm, v(-1.18, -32.17) * mm, v(-1.58, -31.8) * mm, v(-2.22, -31.05) * mm]});
            skFitSpline(sketch, "E589", {"points": [v(-2.22, -31.05) * mm, v(-2.76, -30.47) * mm, v(-3.17, -30.18) * mm, v(-3.44, -30.18) * mm]});
            skFitSpline(sketch, "E590", {"points": [v(-3.44, -30.18) * mm, v(-3.72, -30.18) * mm, v(-3.87, -30.47) * mm, v(-3.87, -31.07) * mm]});
            skFitSpline(sketch, "E591", {"points": [v(-3.87, -31.07) * mm, v(-3.87, -31.6) * mm, v(-3.78, -32.28) * mm, v(-3.6, -33.1) * mm]});
            skFitSpline(sketch, "E592", {"points": [v(-3.6, -33.1) * mm, v(-3.43, -33.93) * mm, v(-3.2, -34.56) * mm, v(-2.94, -35) * mm]});
            skFitSpline(sketch, "E593", {"points": [v(-2.94, -35) * mm, v(-2.68, -35.43) * mm, v(-2.37, -35.65) * mm, v(-2, -35.65) * mm]});
            skFitSpline(sketch, "E594", {"points": [v(-2, -35.65) * mm, v(-1.7, -35.65) * mm, v(-1.34, -35.52) * mm, v(-0.94, -35.28) * mm]});
            skFitSpline(sketch, "E595", {"points": [v(-10.8, -29.33) * mm, v(-10.91, -29.28) * mm, v(-11, -29.19) * mm, v(-11.07, -29.06) * mm]});
            skFitSpline(sketch, "E596", {"points": [v(-11.07, -29.06) * mm, v(-11.14, -28.94) * mm, v(-11.18, -28.82) * mm, v(-11.18, -28.72) * mm]});
            skFitSpline(sketch, "E597", {"points": [v(-11.18, -28.72) * mm, v(-11.18, -28.52) * mm, v(-10.98, -28.42) * mm, v(-10.6, -28.42) * mm]});
            skFitSpline(sketch, "E598", {"points": [v(-9.12, -28.55) * mm, v(-8.77, -28.55) * mm, v(-8.44, -28.64) * mm, v(-8.13, -28.8) * mm]});
            skFitSpline(sketch, "E599", {"points": [v(-8.13, -28.8) * mm, v(-7.82, -28.96) * mm, v(-7.48, -29.24) * mm, v(-7.1, -29.65) * mm]});
            skFitSpline(sketch, "E600", {"points": [v(-7.1, -29.65) * mm, v(-6.73, -30.06) * mm, v(-6.44, -30.54) * mm, v(-6.23, -31.09) * mm]});
            skFitSpline(sketch, "E601", {"points": [v(-6.23, -31.09) * mm, v(-6.03, -31.63) * mm, v(-5.88, -32.08) * mm, v(-5.79, -32.43) * mm]});
            skFitSpline(sketch, "E602", {"points": [v(-5.79, -32.43) * mm, v(-5.7, -32.78) * mm, v(-5.63, -33.1) * mm, v(-5.58, -33.38) * mm]});
            skFitSpline(sketch, "E603", {"points": [v(-5.58, -33.38) * mm, v(-5.54, -33.67) * mm, v(-5.5, -33.9) * mm, v(-5.5, -34.1) * mm]});
            skFitSpline(sketch, "E604", {"points": [v(-5.5, -34.1) * mm, v(-5.48, -34.28) * mm, v(-5.48, -34.42) * mm, v(-5.48, -34.5) * mm]});
            skFitSpline(sketch, "E605", {"points": [v(-5.48, -34.5) * mm, v(-5.48, -35.53) * mm, v(-5.76, -36.04) * mm, v(-6.33, -36.04) * mm]});
            skFitSpline(sketch, "E606", {"points": [v(-6.33, -36.04) * mm, v(-6.86, -36.04) * mm, v(-7.6, -35.55) * mm, v(-8.54, -34.56) * mm]});
            skFitSpline(sketch, "E607", {"points": [v(-9.2, -33.84) * mm, v(-9.4, -33.63) * mm, v(-9.57, -33.42) * mm, v(-9.7, -33.2) * mm]});
            skFitSpline(sketch, "E608", {"points": [v(-9.7, -33.2) * mm, v(-9.83, -32.97) * mm, v(-9.9, -32.75) * mm, v(-9.9, -32.53) * mm]});
            skFitSpline(sketch, "E609", {"points": [v(-9.9, -32.53) * mm, v(-9.9, -32.47) * mm, v(-9.87, -32.39) * mm, v(-9.82, -32.3) * mm]});
            skFitSpline(sketch, "E610", {"points": [v(-9.37, -32.84) * mm, v(-9.1, -33.22) * mm, v(-8.78, -33.61) * mm, v(-8.4, -34) * mm]});
            skFitSpline(sketch, "E611", {"points": [v(-8.4, -34) * mm, v(-8.03, -34.4) * mm, v(-7.7, -34.6) * mm, v(-7.43, -34.6) * mm]});
            skFitSpline(sketch, "E612", {"points": [v(-7.43, -34.6) * mm, v(-7.11, -34.6) * mm, v(-6.95, -34.26) * mm, v(-6.95, -33.58) * mm]});
            skFitSpline(sketch, "E613", {"points": [v(-6.95, -33.58) * mm, v(-6.95, -33.1) * mm, v(-7.02, -32.5) * mm, v(-7.15, -31.8) * mm]});
            skFitSpline(sketch, "E614", {"points": [v(-7.15, -31.8) * mm, v(-7.29, -31.1) * mm, v(-7.44, -30.58) * mm, v(-7.62, -30.24) * mm]});
            skFitSpline(sketch, "E615", {"points": [v(-7.62, -30.24) * mm, v(-7.8, -29.9) * mm, v(-7.98, -29.68) * mm, v(-8.18, -29.57) * mm]});
            skFitSpline(sketch, "E616", {"points": [v(-8.18, -29.57) * mm, v(-8.38, -29.46) * mm, v(-8.61, -29.4) * mm, v(-8.87, -29.4) * mm]});
            skFitSpline(sketch, "E617", {"points": [v(-11.29, -29.14) * mm, v(-11.29, -28.69) * mm, v(-11.15, -28.46) * mm, v(-10.86, -28.46) * mm]});
            skFitSpline(sketch, "E618", {"points": [v(-10.86, -28.46) * mm, v(-10.7, -28.46) * mm, v(-10.52, -28.55) * mm, v(-10.3, -28.73) * mm]});
            skFitSpline(sketch, "E619", {"points": [v(-10.3, -28.73) * mm, v(-10.11, -28.93) * mm, v(-9.95, -29.18) * mm, v(-9.83, -29.48) * mm]});
            skFitSpline(sketch, "E620", {"points": [v(-9.83, -29.48) * mm, v(-9.7, -29.78) * mm, v(-9.62, -30.05) * mm, v(-9.57, -30.28) * mm]});
            skFitSpline(sketch, "E621", {"points": [v(-9.57, -30.28) * mm, v(-9.52, -30.5) * mm, v(-9.48, -30.78) * mm, v(-9.46, -31.1) * mm]});
            skFitSpline(sketch, "E622", {"points": [v(-8.99, -35.3) * mm, v(-8.99, -35.79) * mm, v(-9.1, -36.03) * mm, v(-9.32, -36.03) * mm]});
            skFitSpline(sketch, "E623", {"points": [v(-9.32, -36.03) * mm, v(-9.52, -36.03) * mm, v(-9.8, -35.88) * mm, v(-10.17, -35.6) * mm]});
            skFitSpline(sketch, "E624", {"points": [v(-10.17, -35.6) * mm, v(-10.53, -35.35) * mm, v(-11.12, -34.87) * mm, v(-11.93, -34.14) * mm]});
            skFitSpline(sketch, "E625", {"points": [v(-11.93, -34.14) * mm, v(-11.99, -34.08) * mm, v(-12.02, -34.03) * mm, v(-12.05, -33.99) * mm]});
            skFitSpline(sketch, "E626", {"points": [v(-12.05, -33.99) * mm, v(-12.08, -33.95) * mm, v(-12.1, -33.91) * mm, v(-12.1, -33.87) * mm]});
            skFitSpline(sketch, "E627", {"points": [v(-12.1, -33.87) * mm, v(-12.1, -33.85) * mm, v(-12.08, -33.81) * mm, v(-12.01, -33.78) * mm]});
            skFitSpline(sketch, "E628", {"points": [v(-12.01, -33.78) * mm, v(-11.92, -33.78) * mm, v(-11.8, -33.82) * mm, v(-11.67, -33.91) * mm]});
            skFitSpline(sketch, "E629", {"points": [v(-11.67, -33.91) * mm, v(-11.54, -34) * mm, v(-11.41, -34.1) * mm, v(-11.3, -34.18) * mm]});
            skFitSpline(sketch, "E630", {"points": [v(-11.3, -34.18) * mm, v(-11.18, -34.27) * mm, v(-11.07, -34.36) * mm, v(-10.98, -34.45) * mm]});
            skFitSpline(sketch, "E631", {"points": [v(-10.58, -34.75) * mm, v(-10.56, -34.73) * mm, v(-10.55, -34.71) * mm, v(-10.53, -34.68) * mm]});
            skFitSpline(sketch, "E632", {"points": [v(-10.53, -34.68) * mm, v(-10.5, -34.65) * mm, v(-10.5, -34.6) * mm, v(-10.5, -34.51) * mm]});
            skFitSpline(sketch, "E633", {"points": [v(-15.04, -33.96) * mm, v(-14.75, -34.25) * mm, v(-14.54, -34.4) * mm, v(-14.4, -34.4) * mm]});
            skFitSpline(sketch, "E634", {"points": [v(-14.4, -34.4) * mm, v(-14.24, -34.4) * mm, v(-14.16, -34.18) * mm, v(-14.16, -33.74) * mm]});
            skFitSpline(sketch, "E635", {"points": [v(-15.08, -27.43) * mm, v(-15.46, -25.24) * mm, v(-15.66, -23.89) * mm, v(-15.66, -23.38) * mm]});
            skFitSpline(sketch, "E636", {"points": [v(-15.66, -23.38) * mm, v(-15.66, -22.98) * mm, v(-15.57, -22.78) * mm, v(-15.39, -22.78) * mm]});
            skFitSpline(sketch, "E637", {"points": [v(-15.39, -22.78) * mm, v(-15.26, -22.78) * mm, v(-15.13, -22.83) * mm, v(-15, -22.92) * mm]});
            skFitSpline(sketch, "E638", {"points": [v(-14.03, -23.56) * mm, v(-13.56, -23.88) * mm, v(-13.19, -24.12) * mm, v(-12.9, -24.28) * mm]});
            skFitSpline(sketch, "E639", {"points": [v(-12.9, -24.28) * mm, v(-12.62, -24.44) * mm, v(-12.48, -24.6) * mm, v(-12.48, -24.72) * mm]});
            skFitSpline(sketch, "E640", {"points": [v(-12.48, -24.72) * mm, v(-12.5, -24.82) * mm, v(-12.55, -24.87) * mm, v(-12.63, -24.87) * mm]});
            skFitSpline(sketch, "E641", {"points": [v(-12.86, -24.8) * mm, v(-13.36, -24.5) * mm, v(-13.64, -24.35) * mm, v(-13.72, -24.35) * mm]});
            skFitSpline(sketch, "E642", {"points": [v(-13.72, -24.35) * mm, v(-13.85, -24.35) * mm, v(-13.91, -24.49) * mm, v(-13.91, -24.76) * mm]});
            skFitSpline(sketch, "E643", {"points": [v(-12.55, -35.39) * mm, v(-12.55, -35.9) * mm, v(-12.67, -36.16) * mm, v(-12.9, -36.16) * mm]});
            skFitSpline(sketch, "E644", {"points": [v(-12.9, -36.16) * mm, v(-13.25, -36.16) * mm, v(-13.82, -35.77) * mm, v(-14.6, -35) * mm]});
            skFitSpline(sketch, "E645", {"points": [v(-14.6, -35) * mm, v(-15.37, -34.22) * mm, v(-15.75, -33.78) * mm, v(-15.75, -33.66) * mm]});
            skFitSpline(sketch, "E646", {"points": [v(-15.75, -33.66) * mm, v(-15.75, -33.57) * mm, v(-15.7, -33.52) * mm, v(-15.6, -33.52) * mm]});
            skFitSpline(sketch, "E647", {"points": [v(-15.6, -33.52) * mm, v(-15.5, -33.52) * mm, v(-15.32, -33.67) * mm, v(-15.04, -33.96) * mm]});
            skFitSpline(sketch, "E648", {"points": [v(-18.37, -28.75) * mm, v(-17.76, -28.96) * mm, v(-17.33, -29.2) * mm, v(-17.05, -29.48) * mm]});
            skFitSpline(sketch, "E649", {"points": [v(-17.05, -29.48) * mm, v(-16.78, -29.75) * mm, v(-16.52, -30.34) * mm, v(-16.26, -31.23) * mm]});
            skFitSpline(sketch, "E650", {"points": [v(-16.26, -31.23) * mm, v(-16, -32.12) * mm, v(-15.87, -32.85) * mm, v(-15.87, -33.43) * mm]});
            skFitSpline(sketch, "E651", {"points": [v(-15.87, -33.43) * mm, v(-15.87, -34.16) * mm, v(-16.02, -34.78) * mm, v(-16.32, -35.3) * mm]});
            skFitSpline(sketch, "E652", {"points": [v(-16.32, -35.3) * mm, v(-16.61, -35.8) * mm, v(-17.03, -36.06) * mm, v(-17.56, -36.06) * mm]});
            skFitSpline(sketch, "E653", {"points": [v(-17.56, -36.06) * mm, v(-18.1, -36.06) * mm, v(-18.62, -35.9) * mm, v(-19.13, -35.54) * mm]});
            skFitSpline(sketch, "E654", {"points": [v(-20.12, -34.9) * mm, v(-20.3, -34.79) * mm, v(-20.45, -34.68) * mm, v(-20.58, -34.57) * mm]});
            skFitSpline(sketch, "E655", {"points": [v(-20.58, -34.57) * mm, v(-20.71, -34.46) * mm, v(-20.84, -34.34) * mm, v(-20.97, -34.2) * mm]});
            skFitSpline(sketch, "E656", {"points": [v(-20.97, -34.2) * mm, v(-21.1, -34.08) * mm, v(-21.2, -33.86) * mm, v(-21.26, -33.55) * mm]});
            skFitSpline(sketch, "E657", {"points": [v(-21.79, -30.84) * mm, v(-21.79, -30.26) * mm, v(-21.54, -29.7) * mm, v(-21.06, -29.17) * mm]});
            skFitSpline(sketch, "E658", {"points": [v(-21.06, -29.17) * mm, v(-20.57, -28.63) * mm, v(-20.16, -28.37) * mm, v(-19.8, -28.37) * mm]});
            skFitSpline(sketch, "E659", {"points": [v(-18, -30.05) * mm, v(-18.1, -29.8) * mm, v(-18.2, -29.6) * mm, v(-18.3, -29.45) * mm]});
            skFitSpline(sketch, "E660", {"points": [v(-18.3, -29.45) * mm, v(-18.42, -29.32) * mm, v(-18.52, -29.24) * mm, v(-18.58, -29.2) * mm]});
            skFitSpline(sketch, "E661", {"points": [v(-18.58, -29.2) * mm, v(-18.63, -29.16) * mm, v(-18.7, -29.11) * mm, v(-18.79, -29.05) * mm]});
            skFitSpline(sketch, "E662", {"points": [v(-18.79, -29.05) * mm, v(-18.87, -29) * mm, v(-18.97, -28.97) * mm, v(-19.1, -28.97) * mm]});
            skFitSpline(sketch, "E663", {"points": [v(-19.1, -28.97) * mm, v(-19.3, -28.97) * mm, v(-19.5, -29.07) * mm, v(-19.68, -29.29) * mm]});
            skFitSpline(sketch, "E664", {"points": [v(-19.68, -29.29) * mm, v(-19.86, -29.5) * mm, v(-19.96, -29.73) * mm, v(-20, -29.97) * mm]});
            skFitSpline(sketch, "E665", {"points": [v(-20, -29.97) * mm, v(-20.1, -30.43) * mm, v(-20.16, -30.87) * mm, v(-20.16, -31.31) * mm]});
            skFitSpline(sketch, "E666", {"points": [v(-20.16, -31.31) * mm, v(-20.16, -32.05) * mm, v(-20.07, -32.74) * mm, v(-19.9, -33.39) * mm]});
            skFitSpline(sketch, "E667", {"points": [v(-19.9, -33.39) * mm, v(-19.74, -34.03) * mm, v(-19.53, -34.46) * mm, v(-19.3, -34.68) * mm]});
            skFitSpline(sketch, "E668", {"points": [v(-19.3, -34.68) * mm, v(-19.05, -34.9) * mm, v(-18.89, -35) * mm, v(-18.8, -35) * mm]});
            skFitSpline(sketch, "E669", {"points": [v(-18.8, -35) * mm, v(-18.64, -35) * mm, v(-18.45, -34.92) * mm, v(-18.2, -34.77) * mm]});
            skFitSpline(sketch, "E670", {"points": [v(-18.2, -34.77) * mm, v(-17.97, -34.61) * mm, v(-17.78, -34.33) * mm, v(-17.65, -33.91) * mm]});
            skFitSpline(sketch, "E671", {"points": [v(-17.65, -33.91) * mm, v(-17.5, -33.5) * mm, v(-17.44, -33.04) * mm, v(-17.44, -32.53) * mm]});
            skFitSpline(sketch, "E672", {"points": [v(-17.44, -32.53) * mm, v(-17.44, -32.15) * mm, v(-17.47, -31.86) * mm, v(-17.54, -31.66) * mm]});
            skFitSpline(sketch, "E673", {"points": [v(-24.75, -28.75) * mm, v(-24.15, -28.96) * mm, v(-23.7, -29.2) * mm, v(-23.43, -29.48) * mm]});
            skFitSpline(sketch, "E674", {"points": [v(-23.43, -29.48) * mm, v(-23.16, -29.75) * mm, v(-22.9, -30.34) * mm, v(-22.64, -31.23) * mm]});
            skFitSpline(sketch, "E675", {"points": [v(-22.64, -31.23) * mm, v(-22.38, -32.12) * mm, v(-22.25, -32.85) * mm, v(-22.25, -33.43) * mm]});
            skFitSpline(sketch, "E676", {"points": [v(-22.25, -33.43) * mm, v(-22.25, -34.16) * mm, v(-22.4, -34.78) * mm, v(-22.7, -35.3) * mm]});
            skFitSpline(sketch, "E677", {"points": [v(-22.7, -35.3) * mm, v(-23, -35.8) * mm, v(-23.4, -36.06) * mm, v(-23.94, -36.06) * mm]});
            skFitSpline(sketch, "E678", {"points": [v(-23.94, -36.06) * mm, v(-24.48, -36.06) * mm, v(-25, -35.9) * mm, v(-25.5, -35.54) * mm]});
            skFitSpline(sketch, "E679", {"points": [v(-26.5, -34.9) * mm, v(-26.68, -34.79) * mm, v(-26.83, -34.68) * mm, v(-26.96, -34.57) * mm]});
            skFitSpline(sketch, "E680", {"points": [v(-26.96, -34.57) * mm, v(-27.1, -34.46) * mm, v(-27.22, -34.34) * mm, v(-27.35, -34.2) * mm]});
            skFitSpline(sketch, "E681", {"points": [v(-27.35, -34.2) * mm, v(-27.48, -34.08) * mm, v(-27.58, -33.86) * mm, v(-27.64, -33.55) * mm]});
            skFitSpline(sketch, "E682", {"points": [v(-28.17, -30.84) * mm, v(-28.17, -30.26) * mm, v(-27.92, -29.7) * mm, v(-27.44, -29.17) * mm]});
            skFitSpline(sketch, "E683", {"points": [v(-27.44, -29.17) * mm, v(-26.95, -28.63) * mm, v(-26.54, -28.37) * mm, v(-26.19, -28.37) * mm]});
            skFitSpline(sketch, "E684", {"points": [v(-24.38, -30.05) * mm, v(-24.48, -29.8) * mm, v(-24.57, -29.6) * mm, v(-24.68, -29.45) * mm]});
            skFitSpline(sketch, "E685", {"points": [v(-24.68, -29.45) * mm, v(-24.8, -29.32) * mm, v(-24.9, -29.24) * mm, v(-24.96, -29.2) * mm]});
            skFitSpline(sketch, "E686", {"points": [v(-24.96, -29.2) * mm, v(-25.02, -29.16) * mm, v(-25.09, -29.11) * mm, v(-25.17, -29.05) * mm]});
            skFitSpline(sketch, "E687", {"points": [v(-25.17, -29.05) * mm, v(-25.25, -29) * mm, v(-25.35, -28.97) * mm, v(-25.47, -28.97) * mm]});
            skFitSpline(sketch, "E688", {"points": [v(-25.47, -28.97) * mm, v(-25.7, -28.97) * mm, v(-25.89, -29.07) * mm, v(-26.06, -29.29) * mm]});
            skFitSpline(sketch, "E689", {"points": [v(-26.06, -29.29) * mm, v(-26.24, -29.5) * mm, v(-26.34, -29.73) * mm, v(-26.38, -29.97) * mm]});
            skFitSpline(sketch, "E690", {"points": [v(-26.38, -29.97) * mm, v(-26.49, -30.43) * mm, v(-26.54, -30.87) * mm, v(-26.54, -31.31) * mm]});
            skFitSpline(sketch, "E691", {"points": [v(-26.54, -31.31) * mm, v(-26.54, -32.05) * mm, v(-26.45, -32.74) * mm, v(-26.29, -33.39) * mm]});
            skFitSpline(sketch, "E692", {"points": [v(-26.29, -33.39) * mm, v(-26.12, -34.03) * mm, v(-25.91, -34.46) * mm, v(-25.67, -34.68) * mm]});
            skFitSpline(sketch, "E693", {"points": [v(-25.67, -34.68) * mm, v(-25.43, -34.9) * mm, v(-25.27, -35) * mm, v(-25.18, -35) * mm]});
            skFitSpline(sketch, "E694", {"points": [v(-25.18, -35) * mm, v(-25.02, -35) * mm, v(-24.83, -34.92) * mm, v(-24.59, -34.77) * mm]});
            skFitSpline(sketch, "E695", {"points": [v(-24.59, -34.77) * mm, v(-24.35, -34.61) * mm, v(-24.16, -34.33) * mm, v(-24.03, -33.91) * mm]});
            skFitSpline(sketch, "E696", {"points": [v(-24.03, -33.91) * mm, v(-23.9, -33.5) * mm, v(-23.82, -33.04) * mm, v(-23.82, -32.53) * mm]});
            skFitSpline(sketch, "E697", {"points": [v(-23.82, -32.53) * mm, v(-23.82, -32.15) * mm, v(-23.85, -31.86) * mm, v(-23.92, -31.66) * mm]});
            skFitSpline(sketch, "E698", {"points": [v(-29.49, -30.2) * mm, v(-29.52, -29.94) * mm, v(-29.64, -29.77) * mm, v(-29.82, -29.71) * mm]});
            skFitSpline(sketch, "E699", {"points": [v(-29.82, -29.71) * mm, v(-30.01, -29.65) * mm, v(-30.34, -29.63) * mm, v(-30.82, -29.63) * mm]});
            skFitSpline(sketch, "E700", {"points": [v(-32.6, -29.59) * mm, v(-32.3, -30.26) * mm, v(-31.89, -31) * mm, v(-31.38, -31.82) * mm]});
            skFitSpline(sketch, "E701", {"points": [v(-31.38, -31.82) * mm, v(-30.87, -32.63) * mm, v(-30.37, -33.32) * mm, v(-29.9, -33.87) * mm]});
            skFitSpline(sketch, "E702", {"points": [v(-29.9, -33.87) * mm, v(-29.43, -34.43) * mm, v(-28.81, -35.04) * mm, v(-28.05, -35.7) * mm]});
            skFitSpline(sketch, "E703", {"points": [v(-28.34, -36) * mm, v(-28.77, -35.68) * mm, v(-29.35, -35.2) * mm, v(-30.1, -34.53) * mm]});
            skFitSpline(sketch, "E704", {"points": [v(-30.1, -34.53) * mm, v(-30.84, -33.87) * mm, v(-31.53, -33.1) * mm, v(-32.16, -32.19) * mm]});
            skFitSpline(sketch, "E705", {"points": [v(-34.28, -28.64) * mm, v(-34.3, -28.6) * mm, v(-34.31, -28.54) * mm, v(-34.31, -28.46) * mm]});
            skFitSpline(sketch, "E706", {"points": [v(-34.31, -28.46) * mm, v(-34.31, -28.37) * mm, v(-34.27, -28.33) * mm, v(-34.18, -28.33) * mm]});
            skFitSpline(sketch, "E707", {"points": [v(-34.02, -28.38) * mm, v(-33.87, -28.5) * mm, v(-33.58, -28.56) * mm, v(-33.17, -28.56) * mm]});
            skFitSpline(sketch, "E708", {"points": [v(-30.4, -28.23) * mm, v(-30.06, -28.23) * mm, v(-29.8, -28.29) * mm, v(-29.6, -28.4) * mm]});
            skFitSpline(sketch, "E709", {"points": [v(-29.6, -28.4) * mm, v(-29.4, -28.52) * mm, v(-29.28, -28.65) * mm, v(-29.22, -28.8) * mm]});
            skFitSpline(sketch, "E710", {"points": [v(-29.22, -28.8) * mm, v(-29.17, -28.93) * mm, v(-29.12, -29.12) * mm, v(-29.1, -29.33) * mm]});
            skFitSpline(sketch, "E711", {"points": [v(-29.02, -30) * mm, v(-29.02, -30.4) * mm, v(-29.1, -30.61) * mm, v(-29.23, -30.61) * mm]});
            skFitSpline(sketch, "E712", {"points": [v(-29.23, -30.61) * mm, v(-29.36, -30.61) * mm, v(-29.45, -30.48) * mm, v(-29.49, -30.2) * mm]});
            skFitSpline(sketch, "E713", {"points": [v(-28.22, -35.85) * mm, v(-28.25, -35.88) * mm, v(-28.3, -35.9) * mm, v(-28.4, -35.95) * mm]});
            skFitSpline(sketch, "E714", {"points": [v(-29.27, -35.27) * mm, v(-29.45, -35.15) * mm, v(-29.62, -35.1) * mm, v(-29.78, -35.1) * mm]});
            skFitSpline(sketch, "E715", {"points": [v(-29.78, -35.1) * mm, v(-30.02, -35.1) * mm, v(-30.42, -35.3) * mm, v(-30.96, -35.68) * mm]});
            skFitSpline(sketch, "E716", {"points": [v(-30.96, -35.68) * mm, v(-31.27, -35.94) * mm, v(-31.63, -36.06) * mm, v(-32.03, -36.06) * mm]});
            skFitSpline(sketch, "E717", {"points": [v(-32.03, -36.06) * mm, v(-32.43, -36.06) * mm, v(-32.81, -35.93) * mm, v(-33.19, -35.66) * mm]});
            skFitSpline(sketch, "E718", {"points": [v(-33.19, -35.66) * mm, v(-33.56, -35.4) * mm, v(-33.83, -35.1) * mm, v(-33.98, -34.79) * mm]});
            skFitSpline(sketch, "E719", {"points": [v(-33.98, -34.79) * mm, v(-34.14, -34.47) * mm, v(-34.22, -34.25) * mm, v(-34.22, -34.12) * mm]});
            skFitSpline(sketch, "E720", {"points": [v(-34.22, -34.12) * mm, v(-34.22, -34.07) * mm, v(-34.19, -34.02) * mm, v(-34.12, -33.97) * mm]});
            skFitSpline(sketch, "E721", {"points": [v(-34.12, -33.97) * mm, v(-34, -33.97) * mm, v(-33.9, -34.05) * mm, v(-33.83, -34.22) * mm]});
            skFitSpline(sketch, "E722", {"points": [v(-33.83, -34.22) * mm, v(-33.56, -34.62) * mm, v(-33.23, -34.82) * mm, v(-32.84, -34.82) * mm]});
            skFitSpline(sketch, "E723", {"points": [v(-32.84, -34.82) * mm, v(-32.71, -34.82) * mm, v(-32.6, -34.81) * mm, v(-32.48, -34.78) * mm]});
            skFitSpline(sketch, "E724", {"points": [v(-32.48, -34.78) * mm, v(-32.37, -34.76) * mm, v(-32.25, -34.72) * mm, v(-32.12, -34.67) * mm]});
            skFitSpline(sketch, "E725", {"points": [v(-30.22, -33.8) * mm, v(-30.1, -33.74) * mm, v(-29.98, -33.72) * mm, v(-29.83, -33.72) * mm]});
            skFitSpline(sketch, "E726", {"points": [v(-29.83, -33.72) * mm, v(-29.5, -33.72) * mm, v(-29.2, -33.86) * mm, v(-28.91, -34.13) * mm]});
            skFitSpline(sketch, "E727", {"points": [v(-28.91, -34.13) * mm, v(-28.64, -34.41) * mm, v(-28.45, -34.73) * mm, v(-28.36, -35.08) * mm]});
            skFitSpline(sketch, "E728", {"points": [v(-39.76, -29.33) * mm, v(-39.87, -29.28) * mm, v(-39.95, -29.19) * mm, v(-40.03, -29.06) * mm]});
            skFitSpline(sketch, "E729", {"points": [v(-40.03, -29.06) * mm, v(-40.1, -28.94) * mm, v(-40.13, -28.82) * mm, v(-40.13, -28.72) * mm]});
            skFitSpline(sketch, "E730", {"points": [v(-40.13, -28.72) * mm, v(-40.13, -28.52) * mm, v(-39.94, -28.42) * mm, v(-39.55, -28.42) * mm]});
            skFitSpline(sketch, "E731", {"points": [v(-38.08, -28.55) * mm, v(-37.73, -28.55) * mm, v(-37.4, -28.64) * mm, v(-37.09, -28.8) * mm]});
            skFitSpline(sketch, "E732", {"points": [v(-37.09, -28.8) * mm, v(-36.78, -28.96) * mm, v(-36.43, -29.24) * mm, v(-36.06, -29.65) * mm]});
            skFitSpline(sketch, "E733", {"points": [v(-36.06, -29.65) * mm, v(-35.68, -30.06) * mm, v(-35.4, -30.54) * mm, v(-35.19, -31.09) * mm]});
            skFitSpline(sketch, "E734", {"points": [v(-35.19, -31.09) * mm, v(-34.98, -31.63) * mm, v(-34.83, -32.08) * mm, v(-34.74, -32.43) * mm]});
            skFitSpline(sketch, "E735", {"points": [v(-34.74, -32.43) * mm, v(-34.65, -32.78) * mm, v(-34.58, -33.1) * mm, v(-34.54, -33.38) * mm]});
            skFitSpline(sketch, "E736", {"points": [v(-34.54, -33.38) * mm, v(-34.5, -33.67) * mm, v(-34.46, -33.9) * mm, v(-34.45, -34.1) * mm]});
            skFitSpline(sketch, "E737", {"points": [v(-34.45, -34.1) * mm, v(-34.44, -34.28) * mm, v(-34.43, -34.42) * mm, v(-34.43, -34.5) * mm]});
            skFitSpline(sketch, "E738", {"points": [v(-34.43, -34.5) * mm, v(-34.43, -35.53) * mm, v(-34.71, -36.04) * mm, v(-35.28, -36.04) * mm]});
            skFitSpline(sketch, "E739", {"points": [v(-35.28, -36.04) * mm, v(-35.81, -36.04) * mm, v(-36.55, -35.55) * mm, v(-37.5, -34.56) * mm]});
            skFitSpline(sketch, "E740", {"points": [v(-38.15, -33.84) * mm, v(-38.36, -33.63) * mm, v(-38.53, -33.42) * mm, v(-38.66, -33.2) * mm]});
            skFitSpline(sketch, "E741", {"points": [v(-38.66, -33.2) * mm, v(-38.79, -32.97) * mm, v(-38.85, -32.75) * mm, v(-38.85, -32.53) * mm]});
            skFitSpline(sketch, "E742", {"points": [v(-38.85, -32.53) * mm, v(-38.85, -32.47) * mm, v(-38.83, -32.39) * mm, v(-38.77, -32.3) * mm]});
            skFitSpline(sketch, "E743", {"points": [v(-38.33, -32.84) * mm, v(-38.06, -33.22) * mm, v(-37.73, -33.61) * mm, v(-37.36, -34) * mm]});
            skFitSpline(sketch, "E744", {"points": [v(-37.36, -34) * mm, v(-36.98, -34.4) * mm, v(-36.66, -34.6) * mm, v(-36.39, -34.6) * mm]});
            skFitSpline(sketch, "E745", {"points": [v(-36.39, -34.6) * mm, v(-36.07, -34.6) * mm, v(-35.9, -34.26) * mm, v(-35.9, -33.58) * mm]});
            skFitSpline(sketch, "E746", {"points": [v(-35.9, -33.58) * mm, v(-35.9, -33.1) * mm, v(-35.97, -32.5) * mm, v(-36.1, -31.8) * mm]});
            skFitSpline(sketch, "E747", {"points": [v(-36.1, -31.8) * mm, v(-36.24, -31.1) * mm, v(-36.4, -30.58) * mm, v(-36.57, -30.24) * mm]});
            skFitSpline(sketch, "E748", {"points": [v(-36.57, -30.24) * mm, v(-36.75, -29.9) * mm, v(-36.94, -29.68) * mm, v(-37.14, -29.57) * mm]});
            skFitSpline(sketch, "E749", {"points": [v(-37.14, -29.57) * mm, v(-37.34, -29.46) * mm, v(-37.57, -29.4) * mm, v(-37.82, -29.4) * mm]});
            skFitSpline(sketch, "E750", {"points": [v(-40.24, -29.14) * mm, v(-40.24, -28.69) * mm, v(-40.1, -28.46) * mm, v(-39.82, -28.46) * mm]});
            skFitSpline(sketch, "E751", {"points": [v(-39.82, -28.46) * mm, v(-39.66, -28.46) * mm, v(-39.48, -28.55) * mm, v(-39.26, -28.73) * mm]});
            skFitSpline(sketch, "E752", {"points": [v(-39.26, -28.73) * mm, v(-39.07, -28.93) * mm, v(-38.9, -29.18) * mm, v(-38.79, -29.48) * mm]});
            skFitSpline(sketch, "E753", {"points": [v(-38.79, -29.48) * mm, v(-38.66, -29.78) * mm, v(-38.58, -30.05) * mm, v(-38.53, -30.28) * mm]});
            skFitSpline(sketch, "E754", {"points": [v(-38.53, -30.28) * mm, v(-38.47, -30.5) * mm, v(-38.44, -30.78) * mm, v(-38.41, -31.1) * mm]});
            skFitSpline(sketch, "E755", {"points": [v(-37.94, -35.3) * mm, v(-37.94, -35.79) * mm, v(-38.05, -36.03) * mm, v(-38.27, -36.03) * mm]});
            skFitSpline(sketch, "E756", {"points": [v(-38.27, -36.03) * mm, v(-38.48, -36.03) * mm, v(-38.76, -35.88) * mm, v(-39.12, -35.6) * mm]});
            skFitSpline(sketch, "E757", {"points": [v(-39.12, -35.6) * mm, v(-39.49, -35.35) * mm, v(-40.07, -34.87) * mm, v(-40.89, -34.14) * mm]});
            skFitSpline(sketch, "E758", {"points": [v(-40.89, -34.14) * mm, v(-40.94, -34.08) * mm, v(-40.98, -34.03) * mm, v(-41, -33.99) * mm]});
            skFitSpline(sketch, "E759", {"points": [v(-41, -33.99) * mm, v(-41.03, -33.95) * mm, v(-41.05, -33.91) * mm, v(-41.06, -33.87) * mm]});
            skFitSpline(sketch, "E760", {"points": [v(-41.06, -33.87) * mm, v(-41.06, -33.85) * mm, v(-41.03, -33.81) * mm, v(-40.97, -33.78) * mm]});
            skFitSpline(sketch, "E761", {"points": [v(-40.97, -33.78) * mm, v(-40.88, -33.78) * mm, v(-40.76, -33.82) * mm, v(-40.63, -33.91) * mm]});
            skFitSpline(sketch, "E762", {"points": [v(-40.63, -33.91) * mm, v(-40.5, -34) * mm, v(-40.37, -34.1) * mm, v(-40.25, -34.18) * mm]});
            skFitSpline(sketch, "E763", {"points": [v(-40.25, -34.18) * mm, v(-40.13, -34.27) * mm, v(-40.03, -34.36) * mm, v(-39.94, -34.45) * mm]});
            skFitSpline(sketch, "E764", {"points": [v(-39.53, -34.75) * mm, v(-39.52, -34.73) * mm, v(-39.5, -34.71) * mm, v(-39.48, -34.68) * mm]});
            skFitSpline(sketch, "E765", {"points": [v(-39.48, -34.68) * mm, v(-39.46, -34.65) * mm, v(-39.45, -34.6) * mm, v(-39.45, -34.51) * mm]});
            skFitSpline(sketch, "E766", {"points": [v(22.3, -54) * mm, v(22.86, -53.32) * mm, v(23.74, -52.78) * mm, v(24.93, -52.38) * mm]});
            skFitSpline(sketch, "E767", {"points": [v(24.93, -52.38) * mm, v(25.54, -52.18) * mm, v(26.1, -52.02) * mm, v(26.63, -51.9) * mm]});
            skFitSpline(sketch, "E768", {"points": [v(26.63, -51.9) * mm, v(27.16, -51.8) * mm, v(27.71, -51.68) * mm, v(28.28, -51.56) * mm]});
            skFitSpline(sketch, "E769", {"points": [v(28.28, -51.56) * mm, v(29.15, -51.37) * mm, v(29.75, -51.17) * mm, v(30.06, -50.94) * mm]});
            skFitSpline(sketch, "E770", {"points": [v(30.06, -50.94) * mm, v(30.37, -50.72) * mm, v(30.53, -50.4) * mm, v(30.53, -49.98) * mm]});
            skFitSpline(sketch, "E771", {"points": [v(30.53, -49.98) * mm, v(30.53, -49.7) * mm, v(30.43, -49.45) * mm, v(30.24, -49.23) * mm]});
            skFitSpline(sketch, "E772", {"points": [v(30.24, -49.23) * mm, v(30.04, -49.02) * mm, v(29.8, -48.86) * mm, v(29.54, -48.75) * mm]});
            skFitSpline(sketch, "E773", {"points": [v(29.54, -48.75) * mm, v(29.23, -48.62) * mm, v(28.91, -48.53) * mm, v(28.58, -48.49) * mm]});
            skFitSpline(sketch, "E774", {"points": [v(28.58, -48.49) * mm, v(28.25, -48.44) * mm, v(27.92, -48.42) * mm, v(27.58, -48.42) * mm]});
            skFitSpline(sketch, "E775", {"points": [v(27.58, -48.42) * mm, v(26.63, -48.42) * mm, v(25.7, -48.6) * mm, v(24.8, -48.94) * mm]});
            skFitSpline(sketch, "E776", {"points": [v(24.8, -48.94) * mm, v(23.88, -49.28) * mm, v(23.11, -49.7) * mm, v(22.49, -50.22) * mm]});
            skFitSpline(sketch, "E777", {"points": [v(22.06, -46.56) * mm, v(22.8, -46.25) * mm, v(23.66, -46) * mm, v(24.66, -45.8) * mm]});
            skFitSpline(sketch, "E778", {"points": [v(24.66, -45.8) * mm, v(25.66, -45.6) * mm, v(26.67, -45.5) * mm, v(27.7, -45.5) * mm]});
            skFitSpline(sketch, "E779", {"points": [v(27.7, -45.5) * mm, v(29.74, -45.5) * mm, v(31.41, -45.96) * mm, v(32.71, -46.9) * mm]});
            skFitSpline(sketch, "E780", {"points": [v(32.71, -46.9) * mm, v(34.01, -47.83) * mm, v(34.66, -49.04) * mm, v(34.66, -50.52) * mm]});
            skFitSpline(sketch, "E781", {"points": [v(34.66, -50.52) * mm, v(34.66, -51.62) * mm, v(34.38, -52.55) * mm, v(33.8, -53.29) * mm]});
            skFitSpline(sketch, "E782", {"points": [v(33.8, -53.29) * mm, v(33.23, -54.03) * mm, v(32.28, -54.62) * mm, v(30.97, -55.06) * mm]});
            skFitSpline(sketch, "E783", {"points": [v(30.97, -55.06) * mm, v(30.4, -55.25) * mm, v(29.79, -55.4) * mm, v(29.13, -55.53) * mm]});
            skFitSpline(sketch, "E784", {"points": [v(29.13, -55.53) * mm, v(28.48, -55.66) * mm, v(27.86, -55.79) * mm, v(27.28, -55.93) * mm]});
            skFitSpline(sketch, "E785", {"points": [v(27.28, -55.93) * mm, v(26.72, -56.07) * mm, v(26.3, -56.26) * mm, v(26, -56.51) * mm]});
            skFitSpline(sketch, "E786", {"points": [v(26, -56.51) * mm, v(25.72, -56.77) * mm, v(25.57, -57.07) * mm, v(25.57, -57.42) * mm]});
            skFitSpline(sketch, "E787", {"points": [v(25.57, -57.42) * mm, v(25.57, -57.8) * mm, v(25.67, -58.08) * mm, v(25.87, -58.27) * mm]});
            skFitSpline(sketch, "E788", {"points": [v(25.87, -58.27) * mm, v(26.07, -58.46) * mm, v(26.32, -58.62) * mm, v(26.63, -58.75) * mm]});
            skFitSpline(sketch, "E789", {"points": [v(26.63, -58.75) * mm, v(26.88, -58.85) * mm, v(27.2, -58.92) * mm, v(27.6, -58.96) * mm]});
            skFitSpline(sketch, "E790", {"points": [v(27.6, -58.96) * mm, v(28, -59) * mm, v(28.32, -59.03) * mm, v(28.56, -59.03) * mm]});
            skFitSpline(sketch, "E791", {"points": [v(28.56, -59.03) * mm, v(29.51, -59.03) * mm, v(30.5, -58.85) * mm, v(31.53, -58.48) * mm]});
            skFitSpline(sketch, "E792", {"points": [v(31.53, -58.48) * mm, v(32.56, -58.12) * mm, v(33.49, -57.6) * mm, v(34.32, -56.92) * mm]});
            skFitSpline(sketch, "E793", {"points": [v(34.76, -60.73) * mm, v(33.92, -61.1) * mm, v(33.02, -61.38) * mm, v(32.06, -61.62) * mm]});
            skFitSpline(sketch, "E794", {"points": [v(32.06, -61.62) * mm, v(31.1, -61.85) * mm, v(29.98, -61.96) * mm, v(28.7, -61.96) * mm]});
            skFitSpline(sketch, "E795", {"points": [v(28.7, -61.96) * mm, v(26.46, -61.96) * mm, v(24.7, -61.47) * mm, v(23.4, -60.5) * mm]});
            skFitSpline(sketch, "E796", {"points": [v(23.4, -60.5) * mm, v(22.1, -59.52) * mm, v(21.44, -58.24) * mm, v(21.44, -56.68) * mm]});
            skFitSpline(sketch, "E797", {"points": [v(21.44, -56.68) * mm, v(21.44, -55.58) * mm, v(21.72, -54.7) * mm, v(22.3, -54) * mm]});
            skSolve(sketch);
        }
        {
            var Q0;
            Q0=qSketchRegion(id+"F0",true);
            extrude(context, id + "F2", {"entities" : qUnion([Q0]), "depth" : 0.8 * mm, "offsetDistance" : 25 * mm, "symmetric" : true});
        }
        {
            var Q0;
            Q0=qSketchRegion(id+"F1",true);
            var Q1;
            Q1=makeQuery(id+"F2.opExtrude","CAP_FACE",FACE,{"disambiguationData":[OSD([sQuery(id+"F0.wireOp",EDGE,"E0.bottom"),sQuery(id+"F0.wireOp",EDGE,"E0.top"),sQuery(id+"F0.wireOp",EDGE,"E0.left"),sQuery(id+"F0.wireOp",EDGE,"E0.right"),sQuery(id+"F0.wireOp",EDGE,"E1"),sQuery(id+"F0.wireOp",EDGE,"E2.filletArc"),sQuery(id+"F0.wireOp",EDGE,"E3.filletArc"),sQuery(id+"F0.wireOp",EDGE,"E4.filletArc"),sQuery(id+"F0.wireOp",EDGE,"E5.filletArc")])],"isStart":true});
            extrude(context, id + "F3", {"entities" : qUnion([Q0]), "operationType" : NewBodyOperationType.REMOVE, "endBound" : BoundingType.UP_TO_SURFACE, "oppositeDirection" : true, "depth" : 25 * mm, "endBoundEntityFace" : qUnion([Q1]), "offsetDistance" : 25 * mm});
        }
        {
            var Q0;
            Q0=qSketchRegion(id+"F1",true);
            var Q1;
            {var subQ27=sQuery(id+"F0.wireOp",EDGE,"E4.filletArc");var subQ29=sQuery(id+"F0.wireOp",EDGE,"E0.left");var subQ31=sQuery(id+"F0.wireOp",EDGE,"E0.top");var subQ32=sQuery(id+"F0.wireOp",EDGE,"E0.right");var subQ33=sQuery(id+"F0.wireOp",EDGE,"E1");var subQ34=sQuery(id+"F0.wireOp",EDGE,"E0.bottom");var subQ37=sQuery(id+"F0.wireOp",EDGE,"E2.filletArc");var subQ39=sQuery(id+"F0.wireOp",EDGE,"E5.filletArc");var subQ40=sQuery(id+"F0.wireOp",EDGE,"E3.filletArc");Q1=makeQuery(id+"F3.boolean.opBoolean","SPLIT",FACE,{"disambiguationData":[TD([makeQuery(id+"F2.opExtrude","SWEPT_FACE",FACE,{"disambiguationData":[OSD([subQ34])]})])],"derivedFrom":makeQuery(id+"F2.opExtrude","CAP_FACE",FACE,{"disambiguationData":[OSD([subQ34,subQ31,subQ29,subQ32,subQ33,subQ37,subQ40,subQ27,subQ39])],"isStart":true})});}
            extrude(context, id + "F4", {"entities" : qUnion([Q0]), "endBound" : BoundingType.UP_TO_SURFACE, "oppositeDirection" : true, "depth" : 25 * mm, "endBoundEntityFace" : qUnion([Q1]), "offsetDistance" : 25 * mm});
        }
        {
            var Q0;
            Q0=makeQuery(id+"F2.opExtrude","CAP_FACE",FACE,{"disambiguationData":[OSD([sQuery(id+"F0.wireOp",EDGE,"E0.bottom"),sQuery(id+"F0.wireOp",EDGE,"E0.top"),sQuery(id+"F0.wireOp",EDGE,"E0.left"),sQuery(id+"F0.wireOp",EDGE,"E0.right"),sQuery(id+"F0.wireOp",EDGE,"E1"),sQuery(id+"F0.wireOp",EDGE,"E2.filletArc"),sQuery(id+"F0.wireOp",EDGE,"E3.filletArc"),sQuery(id+"F0.wireOp",EDGE,"E4.filletArc"),sQuery(id+"F0.wireOp",EDGE,"E5.filletArc"),sQuery(id+"F0.wireOp",EDGE,"E6"),sQuery(id+"F0.wireOp",EDGE,"E7.filletArc"),sQuery(id+"F0.wireOp",EDGE,"E8"),sQuery(id+"F0.wireOp",EDGE,"E9.filletArc")])],"isStart":false});
            var sketch = newSketch(context, id + "F5", { "sketchPlane" : qUnion([Q0])});
            skText(sketch, "E798", { "text": "AWOL", "fontName": "AllertaStencil-Regular.ttf"});
            const initialGuessF5  = {"E798": [-0.042, -0.062, 1, 0, 0.0191]};
            skSetInitialGuess(sketch, initialGuessF5);
            skSolve(sketch);
        }
        {
            var Q0;
            Q0=qSketchRegion(id+"F5",true);
            extrude(context, id + "F6", {"entities" : qUnion([Q0]), "operationType" : NewBodyOperationType.ADD, "depth" : 1 * mm, "offsetDistance" : 25 * mm});
        }
    });
